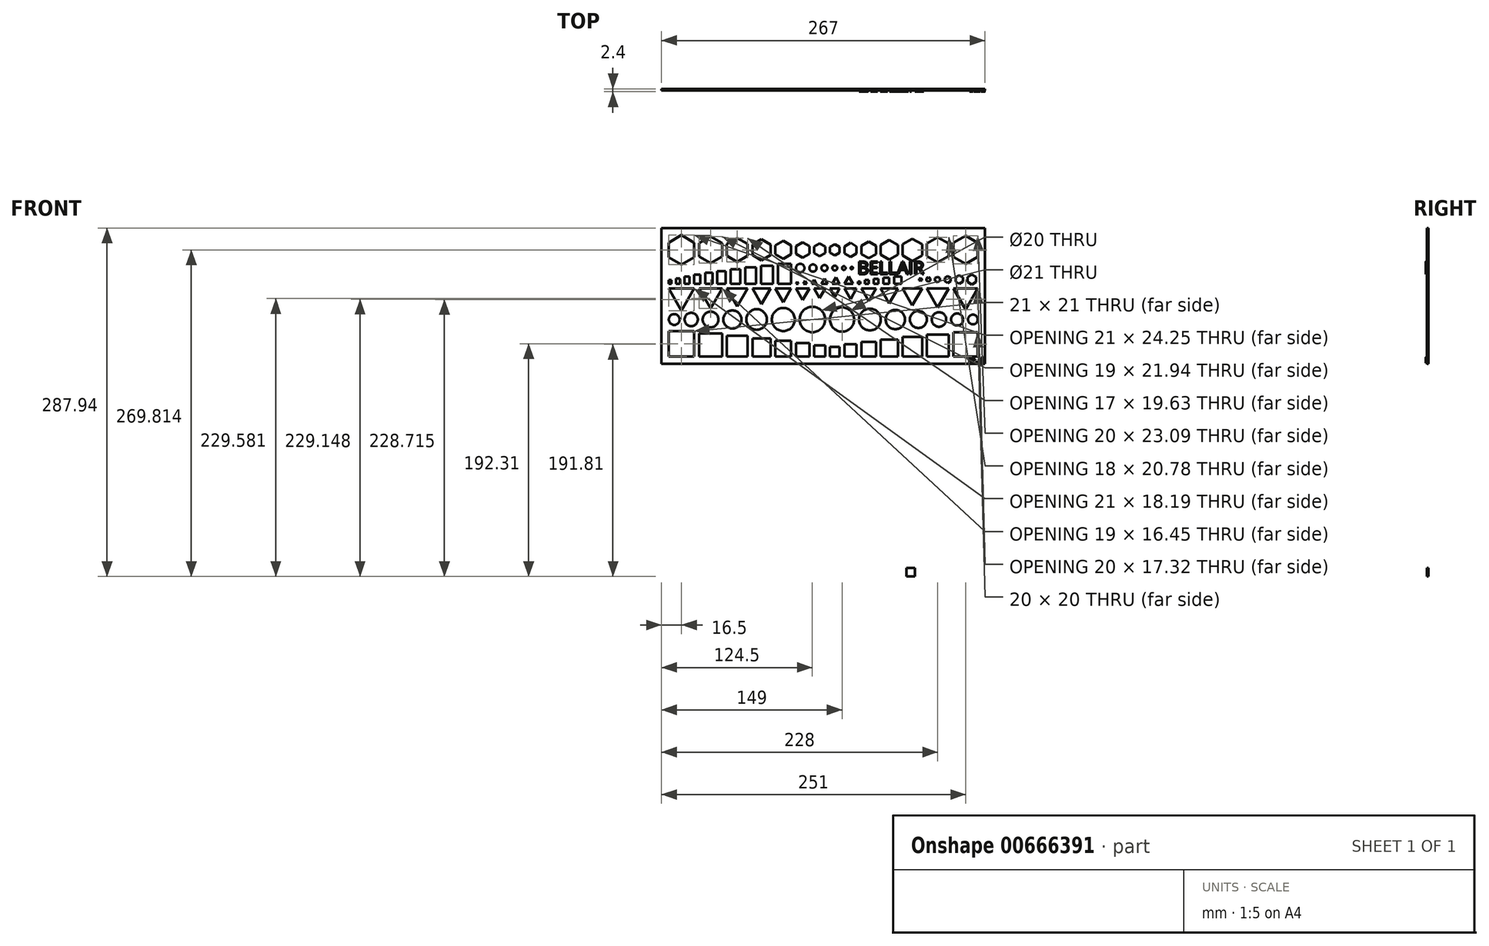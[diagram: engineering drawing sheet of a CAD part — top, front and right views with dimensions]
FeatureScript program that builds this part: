
annotation { "Feature Type Name" : "Feature", "Feature Type Description" : "" }
export const myFeature = defineFeature(function(context is Context, id is Id, definition is map)
    precondition{}
    {
        {
            var Q0;
            Q0=qCreatedBy(makeId("Front.planeOp"),FACE);
            var sketch = newSketch(context, id + "F0", { "sketchPlane" : qUnion([Q0])});
            skLineSegment(sketch, "E0.bottom", {"start": v(0, 0) * mm, "end": v(8, 0) * mm});
            skLineSegment(sketch, "E0.top", {"start": v(0, 8) * mm, "end": v(8, 8) * mm});
            skLineSegment(sketch, "E0.left", {"start": v(0, 0) * mm, "end": v(0, 8) * mm});
            skLineSegment(sketch, "E0.right", {"start": v(8, 0) * mm, "end": v(8, 8) * mm});
            skLineSegment(sketch, "E1.bottom", {"start": v(12, 0) * mm, "end": v(22, 0) * mm});
            skLineSegment(sketch, "E1.top", {"start": v(12, 10) * mm, "end": v(22, 10) * mm});
            skLineSegment(sketch, "E1.left", {"start": v(12, 0) * mm, "end": v(12, 10) * mm});
            skLineSegment(sketch, "E1.right", {"start": v(22, 0) * mm, "end": v(22, 10) * mm});
            skLineSegment(sketch, "E2.bottom", {"start": v(26, 0) * mm, "end": v(38, 0) * mm});
            skLineSegment(sketch, "E2.top", {"start": v(26, 12) * mm, "end": v(38, 12) * mm});
            skLineSegment(sketch, "E2.left", {"start": v(26, 0) * mm, "end": v(26, 12) * mm});
            skLineSegment(sketch, "E2.right", {"start": v(38, 0) * mm, "end": v(38, 12) * mm});
            skLineSegment(sketch, "E3.bottom", {"start": v(42, 0) * mm, "end": v(56, 0) * mm});
            skLineSegment(sketch, "E3.top", {"start": v(42, 14) * mm, "end": v(56, 14) * mm});
            skLineSegment(sketch, "E3.left", {"start": v(42, 0) * mm, "end": v(42, 14) * mm});
            skLineSegment(sketch, "E3.right", {"start": v(56, 0) * mm, "end": v(56, 14) * mm});
            skLineSegment(sketch, "E4.bottom", {"start": v(60, 0) * mm, "end": v(76, 0) * mm});
            skLineSegment(sketch, "E4.top", {"start": v(60, 16) * mm, "end": v(76, 16) * mm});
            skLineSegment(sketch, "E4.left", {"start": v(60, 0) * mm, "end": v(60, 16) * mm});
            skLineSegment(sketch, "E4.right", {"start": v(76, 0) * mm, "end": v(76, 16) * mm});
            skLineSegment(sketch, "E5.bottom", {"start": v(80, 0) * mm, "end": v(98, 0) * mm});
            skLineSegment(sketch, "E5.top", {"start": v(80, 18) * mm, "end": v(98, 18) * mm});
            skLineSegment(sketch, "E5.left", {"start": v(80, 0) * mm, "end": v(80, 18) * mm});
            skLineSegment(sketch, "E5.right", {"start": v(98, 0) * mm, "end": v(98, 18) * mm});
            skLineSegment(sketch, "E6.bottom", {"start": v(102, 0) * mm, "end": v(122, 0) * mm});
            skLineSegment(sketch, "E6.top", {"start": v(102, 20) * mm, "end": v(122, 20) * mm});
            skLineSegment(sketch, "E6.left", {"start": v(102, 0) * mm, "end": v(102, 20) * mm});
            skLineSegment(sketch, "E6.right", {"start": v(122, 0) * mm, "end": v(122, 20) * mm});
            skCircle(sketch, "E7", {"center": v(118, 30.5) * mm, "radius": 4 * mm});
            skCircle(sketch, "E8", {"center": v(105, 30.5) * mm, "radius": 5 * mm});
            skCircle(sketch, "E9", {"center": v(73, 30.5) * mm, "radius": 7 * mm});
            skCircle(sketch, "E10", {"center": v(90, 30.5) * mm, "radius": 6 * mm});
            skCircle(sketch, "E11", {"center": v(54, 30.5) * mm, "radius": 8 * mm});
            skCircle(sketch, "E12", {"center": v(33, 30.5) * mm, "radius": 9 * mm});
            skCircle(sketch, "E13", {"center": v(10, 30.5) * mm, "radius": 10 * mm});
            skLineSegment(sketch, "E14.bottom", {"start": v(-4, 0) * mm, "end": v(-13, 0) * mm});
            skLineSegment(sketch, "E14.top", {"start": v(-4, 9) * mm, "end": v(-13, 9) * mm});
            skLineSegment(sketch, "E14.left", {"start": v(-4, 0) * mm, "end": v(-4, 9) * mm});
            skLineSegment(sketch, "E14.right", {"start": v(-13, 0) * mm, "end": v(-13, 9) * mm});
            skLineSegment(sketch, "E15.bottom", {"start": v(-17, 0) * mm, "end": v(-28, 0) * mm});
            skLineSegment(sketch, "E15.top", {"start": v(-17, 11) * mm, "end": v(-28, 11) * mm});
            skLineSegment(sketch, "E15.left", {"start": v(-17, 0) * mm, "end": v(-17, 11) * mm});
            skLineSegment(sketch, "E15.right", {"start": v(-28, 0) * mm, "end": v(-28, 11) * mm});
            skLineSegment(sketch, "E16.bottom", {"start": v(-32, 0) * mm, "end": v(-45, 0) * mm});
            skLineSegment(sketch, "E16.top", {"start": v(-32, 13) * mm, "end": v(-45, 13) * mm});
            skLineSegment(sketch, "E16.left", {"start": v(-32, 0) * mm, "end": v(-32, 13) * mm});
            skLineSegment(sketch, "E16.right", {"start": v(-45, 0) * mm, "end": v(-45, 13) * mm});
            skLineSegment(sketch, "E17.bottom", {"start": v(-49, 0) * mm, "end": v(-64, 0) * mm});
            skLineSegment(sketch, "E17.top", {"start": v(-49, 15) * mm, "end": v(-64, 15) * mm});
            skLineSegment(sketch, "E17.left", {"start": v(-49, 0) * mm, "end": v(-49, 15) * mm});
            skLineSegment(sketch, "E17.right", {"start": v(-64, 0) * mm, "end": v(-64, 15) * mm});
            skLineSegment(sketch, "E18.bottom", {"start": v(-68, 0) * mm, "end": v(-85, 0) * mm});
            skLineSegment(sketch, "E18.top", {"start": v(-68, 17) * mm, "end": v(-85, 17) * mm});
            skLineSegment(sketch, "E18.left", {"start": v(-68, 0) * mm, "end": v(-68, 17) * mm});
            skLineSegment(sketch, "E18.right", {"start": v(-85, 0) * mm, "end": v(-85, 17) * mm});
            skLineSegment(sketch, "E19.bottom", {"start": v(-89, 0) * mm, "end": v(-108, 0) * mm});
            skLineSegment(sketch, "E19.top", {"start": v(-89, 19) * mm, "end": v(-108, 19) * mm});
            skLineSegment(sketch, "E19.left", {"start": v(-89, 0) * mm, "end": v(-89, 19) * mm});
            skLineSegment(sketch, "E19.right", {"start": v(-108, 0) * mm, "end": v(-108, 19) * mm});
            skLineSegment(sketch, "E20.bottom", {"start": v(-112, 0) * mm, "end": v(-133, 0) * mm});
            skLineSegment(sketch, "E20.top", {"start": v(-112, 21) * mm, "end": v(-133, 21) * mm});
            skLineSegment(sketch, "E20.left", {"start": v(-112, 0) * mm, "end": v(-112, 21) * mm});
            skLineSegment(sketch, "E20.right", {"start": v(-133, 0) * mm, "end": v(-133, 21) * mm});
            skCircle(sketch, "E21", {"center": v(-38.5, 30.5) * mm, "radius": 9.5 * mm});
            skCircle(sketch, "E22", {"center": v(-60.5, 30.5) * mm, "radius": 8.5 * mm});
            skCircle(sketch, "E23", {"center": v(-80.5, 30.5) * mm, "radius": 7.5 * mm});
            skCircle(sketch, "E24", {"center": v(-128.5, 30.5) * mm, "radius": 4.5 * mm});
            skCircle(sketch, "E25", {"center": v(-98.5, 30.5) * mm, "radius": 6.5 * mm});
            skCircle(sketch, "E26", {"center": v(-114.5, 30.5) * mm, "radius": 5.5 * mm});
            skCircle(sketch, "E27", {"center": v(-14.5, 30.5) * mm, "radius": 10.5 * mm});
            skCircle(sketch, "E28.cCircle", {"center": v(4, 53.69) * mm, "radius": 2.3 * mm, "construction": true});
            skLineSegment(sketch, "E28.0", {"start": v(0, 56) * mm, "end": v(8, 56) * mm});
            skLineSegment(sketch, "E28.1", {"start": v(8, 56) * mm, "end": v(4, 49.07) * mm});
            skLineSegment(sketch, "E28.2", {"start": v(4, 49.07) * mm, "end": v(0, 56) * mm});
            skPoint(sketch, "E28.0.midPoint", {"position": v(4, 56) * mm});
            skCircle(sketch, "E29.cCircle", {"center": v(17, 53.11) * mm, "radius": 2.89 * mm, "construction": true});
            skLineSegment(sketch, "E29.0", {"start": v(12, 56) * mm, "end": v(22, 56) * mm});
            skLineSegment(sketch, "E29.1", {"start": v(22, 56) * mm, "end": v(17, 47.34) * mm});
            skLineSegment(sketch, "E29.2", {"start": v(17, 47.34) * mm, "end": v(12, 56) * mm});
            skPoint(sketch, "E29.0.midPoint", {"position": v(17, 56) * mm});
            skCircle(sketch, "E30.cCircle", {"center": v(32, 52.53) * mm, "radius": 3.46 * mm, "construction": true});
            skLineSegment(sketch, "E30.0", {"start": v(26, 56) * mm, "end": v(38, 56) * mm});
            skLineSegment(sketch, "E30.1", {"start": v(38, 56) * mm, "end": v(32, 45.6) * mm});
            skLineSegment(sketch, "E30.2", {"start": v(32, 45.6) * mm, "end": v(26, 56) * mm});
            skPoint(sketch, "E30.0.midPoint", {"position": v(32, 56) * mm});
            skCircle(sketch, "E31.cCircle", {"center": v(49, 51.96) * mm, "radius": 4.04 * mm, "construction": true});
            skLineSegment(sketch, "E31.0", {"start": v(42, 56) * mm, "end": v(56, 56) * mm});
            skLineSegment(sketch, "E31.1", {"start": v(56, 56) * mm, "end": v(49, 43.87) * mm});
            skLineSegment(sketch, "E31.2", {"start": v(49, 43.87) * mm, "end": v(42, 56) * mm});
            skPoint(sketch, "E31.0.midPoint", {"position": v(49, 56) * mm});
            skCircle(sketch, "E32.cCircle", {"center": v(68, 51.38) * mm, "radius": 4.62 * mm, "construction": true});
            skLineSegment(sketch, "E32.0", {"start": v(60, 56) * mm, "end": v(76, 56) * mm});
            skLineSegment(sketch, "E32.1", {"start": v(76, 56) * mm, "end": v(68, 42.14) * mm});
            skLineSegment(sketch, "E32.2", {"start": v(68, 42.14) * mm, "end": v(60, 56) * mm});
            skPoint(sketch, "E32.0.midPoint", {"position": v(68, 56) * mm});
            skCircle(sketch, "E33.cCircle", {"center": v(89, 50.8) * mm, "radius": 5.2 * mm, "construction": true});
            skLineSegment(sketch, "E33.0", {"start": v(80, 56) * mm, "end": v(98, 56) * mm});
            skLineSegment(sketch, "E33.1", {"start": v(98, 56) * mm, "end": v(89, 40.4) * mm});
            skLineSegment(sketch, "E33.2", {"start": v(89, 40.4) * mm, "end": v(80, 56) * mm});
            skPoint(sketch, "E33.0.midPoint", {"position": v(89, 56) * mm});
            skCircle(sketch, "E34.cCircle", {"center": v(112, 50.22) * mm, "radius": 5.77 * mm, "construction": true});
            skLineSegment(sketch, "E34.0", {"start": v(102, 56) * mm, "end": v(122, 56) * mm});
            skLineSegment(sketch, "E34.1", {"start": v(122, 56) * mm, "end": v(112, 38.68) * mm});
            skLineSegment(sketch, "E34.2", {"start": v(112, 38.68) * mm, "end": v(102, 56) * mm});
            skPoint(sketch, "E34.0.midPoint", {"position": v(112, 56) * mm});
            skCircle(sketch, "E35.cCircle", {"center": v(-8.5, 53.4) * mm, "radius": 2.6 * mm, "construction": true});
            skLineSegment(sketch, "E35.0", {"start": v(-13, 56) * mm, "end": v(-4, 56) * mm});
            skLineSegment(sketch, "E35.1", {"start": v(-4, 56) * mm, "end": v(-8.5, 48.2) * mm});
            skLineSegment(sketch, "E35.2", {"start": v(-8.5, 48.2) * mm, "end": v(-13, 56) * mm});
            skPoint(sketch, "E35.0.midPoint", {"position": v(-8.5, 56) * mm});
            skCircle(sketch, "E36.cCircle", {"center": v(-22.5, 52.82) * mm, "radius": 3.18 * mm, "construction": true});
            skLineSegment(sketch, "E36.0", {"start": v(-28, 56) * mm, "end": v(-17, 56) * mm});
            skLineSegment(sketch, "E36.1", {"start": v(-17, 56) * mm, "end": v(-22.5, 46.47) * mm});
            skLineSegment(sketch, "E36.2", {"start": v(-22.5, 46.47) * mm, "end": v(-28, 56) * mm});
            skPoint(sketch, "E36.0.midPoint", {"position": v(-22.5, 56) * mm});
            skCircle(sketch, "E37.cCircle", {"center": v(-38.5, 52.25) * mm, "radius": 3.75 * mm, "construction": true});
            skLineSegment(sketch, "E37.0", {"start": v(-45, 56) * mm, "end": v(-32, 56) * mm});
            skLineSegment(sketch, "E37.1", {"start": v(-32, 56) * mm, "end": v(-38.5, 44.74) * mm});
            skLineSegment(sketch, "E37.2", {"start": v(-38.5, 44.74) * mm, "end": v(-45, 56) * mm});
            skPoint(sketch, "E37.0.midPoint", {"position": v(-38.5, 56) * mm});
            skCircle(sketch, "E38.cCircle", {"center": v(-56.5, 51.67) * mm, "radius": 4.33 * mm, "construction": true});
            skLineSegment(sketch, "E38.0", {"start": v(-64, 56) * mm, "end": v(-49, 56) * mm});
            skLineSegment(sketch, "E38.1", {"start": v(-49, 56) * mm, "end": v(-56.5, 43) * mm});
            skLineSegment(sketch, "E38.2", {"start": v(-56.5, 43) * mm, "end": v(-64, 56) * mm});
            skPoint(sketch, "E38.0.midPoint", {"position": v(-56.5, 56) * mm});
            skCircle(sketch, "E39.cCircle", {"center": v(-76.5, 51.1) * mm, "radius": 4.9 * mm, "construction": true});
            skLineSegment(sketch, "E39.0", {"start": v(-85, 56) * mm, "end": v(-68, 56) * mm});
            skLineSegment(sketch, "E39.1", {"start": v(-68, 56) * mm, "end": v(-76.5, 41.28) * mm});
            skLineSegment(sketch, "E39.2", {"start": v(-76.5, 41.28) * mm, "end": v(-85, 56) * mm});
            skPoint(sketch, "E39.0.midPoint", {"position": v(-76.5, 56) * mm});
            skCircle(sketch, "E40.cCircle", {"center": v(-98.5, 50.51) * mm, "radius": 5.48 * mm, "construction": true});
            skLineSegment(sketch, "E40.0", {"start": v(-108, 56) * mm, "end": v(-89, 56) * mm});
            skLineSegment(sketch, "E40.1", {"start": v(-89, 56) * mm, "end": v(-98.5, 39.54) * mm});
            skLineSegment(sketch, "E40.2", {"start": v(-98.5, 39.54) * mm, "end": v(-108, 56) * mm});
            skPoint(sketch, "E40.0.midPoint", {"position": v(-98.5, 56) * mm});
            skCircle(sketch, "E41.cCircle", {"center": v(-122.5, 49.94) * mm, "radius": 6.06 * mm, "construction": true});
            skLineSegment(sketch, "E41.0", {"start": v(-133, 56) * mm, "end": v(-112, 56) * mm});
            skLineSegment(sketch, "E41.1", {"start": v(-112, 56) * mm, "end": v(-122.5, 37.81) * mm});
            skLineSegment(sketch, "E41.2", {"start": v(-122.5, 37.81) * mm, "end": v(-133, 56) * mm});
            skPoint(sketch, "E41.0.midPoint", {"position": v(-122.5, 56) * mm});
            skLineSegment(sketch, "E42.bottom", {"start": v(-133, 60) * mm, "end": v(-131, 60) * mm});
            skLineSegment(sketch, "E42.top", {"start": v(-133, 63) * mm, "end": v(-131, 63) * mm});
            skLineSegment(sketch, "E42.left", {"start": v(-133, 60) * mm, "end": v(-133, 63) * mm});
            skLineSegment(sketch, "E42.right", {"start": v(-131, 60) * mm, "end": v(-131, 63) * mm});
            skLineSegment(sketch, "E43.bottom", {"start": v(-127, 60) * mm, "end": v(-124, 60) * mm});
            skLineSegment(sketch, "E43.top", {"start": v(-127, 64.5) * mm, "end": v(-124, 64.5) * mm});
            skLineSegment(sketch, "E43.left", {"start": v(-127, 60) * mm, "end": v(-127, 64.5) * mm});
            skLineSegment(sketch, "E43.right", {"start": v(-124, 60) * mm, "end": v(-124, 64.5) * mm});
            skLineSegment(sketch, "E44.bottom", {"start": v(-120, 60) * mm, "end": v(-116, 60) * mm});
            skLineSegment(sketch, "E44.top", {"start": v(-120, 66) * mm, "end": v(-116, 66) * mm});
            skLineSegment(sketch, "E44.left", {"start": v(-120, 60) * mm, "end": v(-120, 66) * mm});
            skLineSegment(sketch, "E44.right", {"start": v(-116, 60) * mm, "end": v(-116, 66) * mm});
            skLineSegment(sketch, "E45.bottom", {"start": v(-112, 60) * mm, "end": v(-107, 60) * mm});
            skLineSegment(sketch, "E45.top", {"start": v(-112, 67.5) * mm, "end": v(-107, 67.5) * mm});
            skLineSegment(sketch, "E45.left", {"start": v(-112, 60) * mm, "end": v(-112, 67.5) * mm});
            skLineSegment(sketch, "E45.right", {"start": v(-107, 60) * mm, "end": v(-107, 67.5) * mm});
            skLineSegment(sketch, "E46.bottom", {"start": v(-103, 60) * mm, "end": v(-97, 60) * mm});
            skLineSegment(sketch, "E46.top", {"start": v(-103, 69) * mm, "end": v(-97, 69) * mm});
            skLineSegment(sketch, "E46.left", {"start": v(-103, 60) * mm, "end": v(-103, 69) * mm});
            skLineSegment(sketch, "E46.right", {"start": v(-97, 60) * mm, "end": v(-97, 69) * mm});
            skLineSegment(sketch, "E47.bottom", {"start": v(-93, 60) * mm, "end": v(-86, 60) * mm});
            skLineSegment(sketch, "E47.top", {"start": v(-93, 70.5) * mm, "end": v(-86, 70.5) * mm});
            skLineSegment(sketch, "E47.left", {"start": v(-93, 60) * mm, "end": v(-93, 70.5) * mm});
            skLineSegment(sketch, "E47.right", {"start": v(-86, 60) * mm, "end": v(-86, 70.5) * mm});
            skLineSegment(sketch, "E48.bottom", {"start": v(-82, 60) * mm, "end": v(-74, 60) * mm});
            skLineSegment(sketch, "E48.top", {"start": v(-82, 72) * mm, "end": v(-74, 72) * mm});
            skLineSegment(sketch, "E48.left", {"start": v(-82, 60) * mm, "end": v(-82, 72) * mm});
            skLineSegment(sketch, "E48.right", {"start": v(-74, 60) * mm, "end": v(-74, 72) * mm});
            skLineSegment(sketch, "E49.bottom", {"start": v(-70, 60) * mm, "end": v(-61, 60) * mm});
            skLineSegment(sketch, "E49.top", {"start": v(-70, 73.5) * mm, "end": v(-61, 73.5) * mm});
            skLineSegment(sketch, "E49.left", {"start": v(-70, 60) * mm, "end": v(-70, 73.5) * mm});
            skLineSegment(sketch, "E49.right", {"start": v(-61, 60) * mm, "end": v(-61, 73.5) * mm});
            skLineSegment(sketch, "E50.bottom", {"start": v(-57, 60) * mm, "end": v(-47, 60) * mm});
            skLineSegment(sketch, "E50.top", {"start": v(-57, 75) * mm, "end": v(-47, 75) * mm});
            skLineSegment(sketch, "E50.left", {"start": v(-57, 60) * mm, "end": v(-57, 75) * mm});
            skLineSegment(sketch, "E50.right", {"start": v(-47, 60) * mm, "end": v(-47, 75) * mm});
            skLineSegment(sketch, "E51.bottom", {"start": v(-43, 60) * mm, "end": v(-32, 60) * mm});
            skLineSegment(sketch, "E51.top", {"start": v(-43, 76.5) * mm, "end": v(-32, 76.5) * mm});
            skLineSegment(sketch, "E51.left", {"start": v(-43, 60) * mm, "end": v(-43, 76.5) * mm});
            skLineSegment(sketch, "E51.right", {"start": v(-32, 60) * mm, "end": v(-32, 76.5) * mm});
            skCircle(sketch, "E52.cCircle", {"center": v(-27, 60.58) * mm, "radius": 0.58 * mm, "construction": true});
            skLineSegment(sketch, "E52.0", {"start": v(-26, 60) * mm, "end": v(-28, 60) * mm});
            skLineSegment(sketch, "E52.1", {"start": v(-28, 60) * mm, "end": v(-27, 61.73) * mm});
            skLineSegment(sketch, "E52.2", {"start": v(-27, 61.73) * mm, "end": v(-26, 60) * mm});
            skPoint(sketch, "E52.0.midPoint", {"position": v(-27, 60) * mm});
            skCircle(sketch, "E53.cCircle", {"center": v(-20.5, 60.86) * mm, "radius": 0.87 * mm, "construction": true});
            skPoint(sketch, "E53.cCircle.perimeterSnap0", {"position": v(-5.5, 60) * mm});
            skLineSegment(sketch, "E53.0", {"start": v(-19, 60) * mm, "end": v(-22, 60) * mm});
            skLineSegment(sketch, "E53.1", {"start": v(-22, 60) * mm, "end": v(-20.5, 62.6) * mm});
            skLineSegment(sketch, "E53.2", {"start": v(-20.5, 62.6) * mm, "end": v(-19, 60) * mm});
            skPoint(sketch, "E53.0.midPoint", {"position": v(-20.5, 60) * mm});
            skPoint(sketch, "E53.0.midPoint.positionSnap0", {"position": v(-5.5, 60) * mm});
            skCircle(sketch, "E54.cCircle", {"center": v(-13, 61.15) * mm, "radius": 1.15 * mm, "construction": true});
            skLineSegment(sketch, "E54.0", {"start": v(-11, 60) * mm, "end": v(-15, 60) * mm});
            skLineSegment(sketch, "E54.1", {"start": v(-15, 60) * mm, "end": v(-13, 63.46) * mm});
            skLineSegment(sketch, "E54.2", {"start": v(-13, 63.46) * mm, "end": v(-11, 60) * mm});
            skPoint(sketch, "E54.0.midPoint", {"position": v(-13, 60) * mm});
            skCircle(sketch, "E55.cCircle", {"center": v(-4.5, 61.44) * mm, "radius": 1.44 * mm, "construction": true});
            skLineSegment(sketch, "E55.0", {"start": v(-2, 60) * mm, "end": v(-7, 60) * mm});
            skLineSegment(sketch, "E55.1", {"start": v(-7, 60) * mm, "end": v(-4.5, 64.33) * mm});
            skLineSegment(sketch, "E55.2", {"start": v(-4.5, 64.33) * mm, "end": v(-2, 60) * mm});
            skPoint(sketch, "E55.0.midPoint", {"position": v(-4.5, 60) * mm});
            skCircle(sketch, "E56.cCircle", {"center": v(5, 61.73) * mm, "radius": 1.73 * mm, "construction": true});
            skLineSegment(sketch, "E56.0", {"start": v(8, 60) * mm, "end": v(2, 60) * mm});
            skLineSegment(sketch, "E56.1", {"start": v(2, 60) * mm, "end": v(5, 65.2) * mm});
            skLineSegment(sketch, "E56.2", {"start": v(5, 65.2) * mm, "end": v(8, 60) * mm});
            skPoint(sketch, "E56.0.midPoint", {"position": v(5, 60) * mm});
            skCircle(sketch, "E57.cCircle", {"center": v(15.5, 62.02) * mm, "radius": 2.02 * mm, "construction": true});
            skLineSegment(sketch, "E57.0", {"start": v(19, 60) * mm, "end": v(12, 60) * mm});
            skLineSegment(sketch, "E57.1", {"start": v(12, 60) * mm, "end": v(15.5, 66.06) * mm});
            skLineSegment(sketch, "E57.2", {"start": v(15.5, 66.06) * mm, "end": v(19, 60) * mm});
            skPoint(sketch, "E57.0.midPoint", {"position": v(15.5, 60) * mm});
            skLineSegment(sketch, "E58", {"start": v(-28, 60) * mm, "end": v(-28, 75.51) * mm});
            skCircle(sketch, "E59", {"center": v(-24.5, 73) * mm, "radius": 3.5 * mm});
            skCircle(sketch, "E60", {"center": v(-14, 73) * mm, "radius": 3 * mm});
            skCircle(sketch, "E61", {"center": v(-4.5, 73) * mm, "radius": 2.5 * mm});
            skCircle(sketch, "E62", {"center": v(4, 73) * mm, "radius": 2 * mm});
            skCircle(sketch, "E63", {"center": v(11.5, 73) * mm, "radius": 1.5 * mm});
            skCircle(sketch, "E64", {"center": v(18, 73) * mm, "radius": 1 * mm});
            skLineSegment(sketch, "E65.bottom", {"start": v(23, 60) * mm, "end": v(25, 60) * mm});
            skLineSegment(sketch, "E65.top", {"start": v(23, 62) * mm, "end": v(25, 62) * mm});
            skLineSegment(sketch, "E65.left", {"start": v(23, 60) * mm, "end": v(23, 62) * mm});
            skLineSegment(sketch, "E65.right", {"start": v(25, 60) * mm, "end": v(25, 62) * mm});
            skLineSegment(sketch, "E66.bottom", {"start": v(29, 60) * mm, "end": v(32, 60) * mm});
            skLineSegment(sketch, "E66.top", {"start": v(29, 63) * mm, "end": v(32, 63) * mm});
            skLineSegment(sketch, "E66.left", {"start": v(29, 60) * mm, "end": v(29, 63) * mm});
            skLineSegment(sketch, "E66.right", {"start": v(32, 60) * mm, "end": v(32, 63) * mm});
            skLineSegment(sketch, "E67.bottom", {"start": v(36, 60) * mm, "end": v(40, 60) * mm});
            skLineSegment(sketch, "E67.top", {"start": v(36, 64) * mm, "end": v(40, 64) * mm});
            skLineSegment(sketch, "E67.left", {"start": v(36, 60) * mm, "end": v(36, 64) * mm});
            skLineSegment(sketch, "E67.right", {"start": v(40, 60) * mm, "end": v(40, 64) * mm});
            skLineSegment(sketch, "E68.bottom", {"start": v(44, 60) * mm, "end": v(49, 60) * mm});
            skLineSegment(sketch, "E68.top", {"start": v(44, 65) * mm, "end": v(49, 65) * mm});
            skLineSegment(sketch, "E68.left", {"start": v(44, 60) * mm, "end": v(44, 65) * mm});
            skLineSegment(sketch, "E68.right", {"start": v(49, 60) * mm, "end": v(49, 65) * mm});
            skLineSegment(sketch, "E69.bottom", {"start": v(53, 60) * mm, "end": v(59, 60) * mm});
            skLineSegment(sketch, "E69.top", {"start": v(53, 66) * mm, "end": v(59, 66) * mm});
            skLineSegment(sketch, "E69.left", {"start": v(53, 60) * mm, "end": v(53, 66) * mm});
            skLineSegment(sketch, "E69.right", {"start": v(59, 60) * mm, "end": v(59, 66) * mm});
            skLineSegment(sketch, "E70.bottom", {"start": v(63, -181.81) * mm, "end": v(70, -181.81) * mm});
            skLineSegment(sketch, "E70.top", {"start": v(63, -174.81) * mm, "end": v(70, -174.81) * mm});
            skLineSegment(sketch, "E70.left", {"start": v(63, -181.81) * mm, "end": v(63, -174.81) * mm});
            skLineSegment(sketch, "E70.right", {"start": v(70, -181.81) * mm, "end": v(70, -174.81) * mm});
            skCircle(sketch, "E71.cCircle", {"center": v(74.74, 63.5) * mm, "radius": 1 * mm, "construction": true});
            skLineSegment(sketch, "E71.0", {"start": v(75.73, 64.08) * mm, "end": v(75.74, 62.92) * mm});
            skLineSegment(sketch, "E71.1", {"start": v(75.74, 62.92) * mm, "end": v(74.74, 62.34) * mm});
            skLineSegment(sketch, "E71.2", {"start": v(74.74, 62.34) * mm, "end": v(73.74, 62.92) * mm});
            skLineSegment(sketch, "E71.3", {"start": v(73.74, 62.92) * mm, "end": v(73.73, 64.07) * mm});
            skLineSegment(sketch, "E71.4", {"start": v(73.73, 64.07) * mm, "end": v(74.73, 64.65) * mm});
            skLineSegment(sketch, "E71.5", {"start": v(74.73, 64.65) * mm, "end": v(75.73, 64.08) * mm});
            skPoint(sketch, "E71.0.midPoint", {"position": v(75.74, 63.5) * mm});
            skCircle(sketch, "E72.cCircle", {"center": v(81.24, 63.5) * mm, "radius": 1.5 * mm, "construction": true});
            skLineSegment(sketch, "E72.0", {"start": v(82.73, 64.37) * mm, "end": v(82.74, 62.63) * mm});
            skLineSegment(sketch, "E72.1", {"start": v(82.74, 62.63) * mm, "end": v(81.24, 61.77) * mm});
            skLineSegment(sketch, "E72.2", {"start": v(81.24, 61.77) * mm, "end": v(79.74, 62.63) * mm});
            skLineSegment(sketch, "E72.3", {"start": v(79.74, 62.63) * mm, "end": v(79.73, 64.36) * mm});
            skLineSegment(sketch, "E72.4", {"start": v(79.73, 64.36) * mm, "end": v(81.23, 65.23) * mm});
            skLineSegment(sketch, "E72.5", {"start": v(81.23, 65.23) * mm, "end": v(82.73, 64.37) * mm});
            skPoint(sketch, "E72.0.midPoint", {"position": v(82.74, 63.5) * mm});
            skCircle(sketch, "E73.cCircle", {"center": v(88.74, 63.5) * mm, "radius": 2 * mm, "construction": true});
            skLineSegment(sketch, "E73.0", {"start": v(86.74, 62.34) * mm, "end": v(86.73, 64.65) * mm});
            skLineSegment(sketch, "E73.1", {"start": v(86.73, 64.65) * mm, "end": v(88.73, 65.8) * mm});
            skLineSegment(sketch, "E73.2", {"start": v(88.73, 65.8) * mm, "end": v(90.73, 64.66) * mm});
            skLineSegment(sketch, "E73.3", {"start": v(90.73, 64.66) * mm, "end": v(90.74, 62.35) * mm});
            skLineSegment(sketch, "E73.4", {"start": v(90.74, 62.35) * mm, "end": v(88.74, 61.19) * mm});
            skLineSegment(sketch, "E73.5", {"start": v(88.74, 61.19) * mm, "end": v(86.74, 62.34) * mm});
            skPoint(sketch, "E73.0.midPoint", {"position": v(86.74, 63.5) * mm});
            skCircle(sketch, "E74.cCircle", {"center": v(97.24, 63.5) * mm, "radius": 2.5 * mm, "construction": true});
            skLineSegment(sketch, "E74.0", {"start": v(99.73, 64.94) * mm, "end": v(99.74, 62.06) * mm});
            skLineSegment(sketch, "E74.1", {"start": v(99.74, 62.06) * mm, "end": v(97.24, 60.61) * mm});
            skLineSegment(sketch, "E74.2", {"start": v(97.24, 60.61) * mm, "end": v(94.74, 62.05) * mm});
            skLineSegment(sketch, "E74.3", {"start": v(94.74, 62.05) * mm, "end": v(94.73, 64.94) * mm});
            skLineSegment(sketch, "E74.4", {"start": v(94.73, 64.94) * mm, "end": v(97.23, 66.38) * mm});
            skLineSegment(sketch, "E74.5", {"start": v(97.23, 66.38) * mm, "end": v(99.73, 64.94) * mm});
            skPoint(sketch, "E74.0.midPoint", {"position": v(99.74, 63.5) * mm});
            skCircle(sketch, "E75.cCircle", {"center": v(106.74, 63.5) * mm, "radius": 3 * mm, "construction": true});
            skLineSegment(sketch, "E75.0", {"start": v(109.73, 65.23) * mm, "end": v(109.74, 61.77) * mm});
            skLineSegment(sketch, "E75.1", {"start": v(109.74, 61.77) * mm, "end": v(106.74, 60.03) * mm});
            skLineSegment(sketch, "E75.2", {"start": v(106.74, 60.03) * mm, "end": v(103.74, 61.76) * mm});
            skLineSegment(sketch, "E75.3", {"start": v(103.74, 61.76) * mm, "end": v(103.73, 65.23) * mm});
            skLineSegment(sketch, "E75.4", {"start": v(103.73, 65.23) * mm, "end": v(106.73, 66.96) * mm});
            skLineSegment(sketch, "E75.5", {"start": v(106.73, 66.96) * mm, "end": v(109.73, 65.23) * mm});
            skPoint(sketch, "E75.0.midPoint", {"position": v(109.74, 63.5) * mm});
            skCircle(sketch, "E76.cCircle", {"center": v(117.24, 63.5) * mm, "radius": 3.5 * mm, "construction": true});
            skLineSegment(sketch, "E76.0", {"start": v(120.73, 65.52) * mm, "end": v(120.74, 61.48) * mm});
            skLineSegment(sketch, "E76.1", {"start": v(120.74, 61.48) * mm, "end": v(117.24, 59.46) * mm});
            skLineSegment(sketch, "E76.2", {"start": v(117.24, 59.46) * mm, "end": v(113.74, 61.47) * mm});
            skLineSegment(sketch, "E76.3", {"start": v(113.74, 61.47) * mm, "end": v(113.73, 65.51) * mm});
            skLineSegment(sketch, "E76.4", {"start": v(113.73, 65.51) * mm, "end": v(117.23, 67.54) * mm});
            skLineSegment(sketch, "E76.5", {"start": v(117.23, 67.54) * mm, "end": v(120.73, 65.52) * mm});
            skPoint(sketch, "E76.0.midPoint", {"position": v(120.74, 63.5) * mm});
            skCircle(sketch, "E77.cCircle", {"center": v(4, 88) * mm, "radius": 4 * mm, "construction": true});
            skLineSegment(sketch, "E77.0", {"start": v(0, 85.7) * mm, "end": v(0, 90.31) * mm});
            skLineSegment(sketch, "E77.1", {"start": v(0, 90.31) * mm, "end": v(4, 92.62) * mm});
            skLineSegment(sketch, "E77.2", {"start": v(4, 92.62) * mm, "end": v(8, 90.31) * mm});
            skLineSegment(sketch, "E77.3", {"start": v(8, 90.31) * mm, "end": v(8, 85.7) * mm});
            skLineSegment(sketch, "E77.4", {"start": v(8, 85.7) * mm, "end": v(4, 83.38) * mm});
            skLineSegment(sketch, "E77.5", {"start": v(4, 83.38) * mm, "end": v(0, 85.7) * mm});
            skPoint(sketch, "E77.0.midPoint", {"position": v(0, 88) * mm});
            skCircle(sketch, "E78.cCircle", {"center": v(17, 88) * mm, "radius": 5 * mm, "construction": true});
            skLineSegment(sketch, "E78.0", {"start": v(22, 90.9) * mm, "end": v(22, 85.12) * mm});
            skLineSegment(sketch, "E78.1", {"start": v(22, 85.12) * mm, "end": v(17, 82.23) * mm});
            skLineSegment(sketch, "E78.2", {"start": v(17, 82.23) * mm, "end": v(12, 85.12) * mm});
            skLineSegment(sketch, "E78.3", {"start": v(12, 85.12) * mm, "end": v(12, 90.9) * mm});
            skLineSegment(sketch, "E78.4", {"start": v(12, 90.9) * mm, "end": v(17, 93.78) * mm});
            skLineSegment(sketch, "E78.5", {"start": v(17, 93.78) * mm, "end": v(22, 90.9) * mm});
            skPoint(sketch, "E78.0.midPoint", {"position": v(22, 88) * mm});
            skCircle(sketch, "E79.cCircle", {"center": v(32, 88) * mm, "radius": 6 * mm, "construction": true});
            skLineSegment(sketch, "E79.0", {"start": v(26, 84.54) * mm, "end": v(26, 91.47) * mm});
            skLineSegment(sketch, "E79.1", {"start": v(26, 91.47) * mm, "end": v(32, 94.93) * mm});
            skLineSegment(sketch, "E79.2", {"start": v(32, 94.93) * mm, "end": v(38, 91.47) * mm});
            skLineSegment(sketch, "E79.3", {"start": v(38, 91.47) * mm, "end": v(38, 84.54) * mm});
            skLineSegment(sketch, "E79.4", {"start": v(38, 84.54) * mm, "end": v(32, 81.08) * mm});
            skLineSegment(sketch, "E79.5", {"start": v(32, 81.08) * mm, "end": v(26, 84.54) * mm});
            skPoint(sketch, "E79.0.midPoint", {"position": v(26, 88) * mm});
            skCircle(sketch, "E80.cCircle", {"center": v(49, 88) * mm, "radius": 7 * mm, "construction": true});
            skLineSegment(sketch, "E80.0", {"start": v(42, 83.96) * mm, "end": v(42, 92.05) * mm});
            skLineSegment(sketch, "E80.1", {"start": v(42, 92.05) * mm, "end": v(49, 96.09) * mm});
            skLineSegment(sketch, "E80.2", {"start": v(49, 96.09) * mm, "end": v(56, 92.05) * mm});
            skLineSegment(sketch, "E80.3", {"start": v(56, 92.05) * mm, "end": v(56, 83.96) * mm});
            skLineSegment(sketch, "E80.4", {"start": v(56, 83.96) * mm, "end": v(49, 79.92) * mm});
            skLineSegment(sketch, "E80.5", {"start": v(49, 79.92) * mm, "end": v(42, 83.96) * mm});
            skPoint(sketch, "E80.0.midPoint", {"position": v(42, 88) * mm});
            skCircle(sketch, "E81.cCircle", {"center": v(68, 88) * mm, "radius": 8 * mm, "construction": true});
            skLineSegment(sketch, "E81.0", {"start": v(60, 83.38) * mm, "end": v(60, 92.62) * mm});
            skLineSegment(sketch, "E81.1", {"start": v(60, 92.62) * mm, "end": v(68, 97.24) * mm});
            skLineSegment(sketch, "E81.2", {"start": v(68, 97.24) * mm, "end": v(76, 92.62) * mm});
            skLineSegment(sketch, "E81.3", {"start": v(76, 92.62) * mm, "end": v(76, 83.38) * mm});
            skLineSegment(sketch, "E81.4", {"start": v(76, 83.38) * mm, "end": v(68, 78.77) * mm});
            skLineSegment(sketch, "E81.5", {"start": v(68, 78.77) * mm, "end": v(60, 83.38) * mm});
            skPoint(sketch, "E81.0.midPoint", {"position": v(60, 88) * mm});
            skCircle(sketch, "E82.cCircle", {"center": v(89, 88) * mm, "radius": 9 * mm, "construction": true});
            skLineSegment(sketch, "E82.0", {"start": v(80, 82.8) * mm, "end": v(80, 93.2) * mm});
            skLineSegment(sketch, "E82.1", {"start": v(80, 93.2) * mm, "end": v(89, 98.4) * mm});
            skLineSegment(sketch, "E82.2", {"start": v(89, 98.4) * mm, "end": v(98, 93.2) * mm});
            skLineSegment(sketch, "E82.3", {"start": v(98, 93.2) * mm, "end": v(98, 82.8) * mm});
            skLineSegment(sketch, "E82.4", {"start": v(98, 82.8) * mm, "end": v(89, 77.61) * mm});
            skLineSegment(sketch, "E82.5", {"start": v(89, 77.61) * mm, "end": v(80, 82.8) * mm});
            skPoint(sketch, "E82.0.midPoint", {"position": v(80, 88) * mm});
            skCircle(sketch, "E83.cCircle", {"center": v(112, 88) * mm, "radius": 10 * mm, "construction": true});
            skLineSegment(sketch, "E83.0", {"start": v(102, 82.23) * mm, "end": v(102, 93.78) * mm});
            skLineSegment(sketch, "E83.1", {"start": v(102, 93.78) * mm, "end": v(112, 99.55) * mm});
            skLineSegment(sketch, "E83.2", {"start": v(112, 99.55) * mm, "end": v(122, 93.78) * mm});
            skLineSegment(sketch, "E83.3", {"start": v(122, 93.78) * mm, "end": v(122, 82.23) * mm});
            skLineSegment(sketch, "E83.4", {"start": v(122, 82.23) * mm, "end": v(112, 76.46) * mm});
            skLineSegment(sketch, "E83.5", {"start": v(112, 76.46) * mm, "end": v(102, 82.23) * mm});
            skPoint(sketch, "E83.0.midPoint", {"position": v(102, 88) * mm});
            skCircle(sketch, "E84.cCircle", {"center": v(-8.5, 88) * mm, "radius": 4.5 * mm, "construction": true});
            skLineSegment(sketch, "E84.0", {"start": v(-13, 85.4) * mm, "end": v(-13, 90.6) * mm});
            skLineSegment(sketch, "E84.1", {"start": v(-13, 90.6) * mm, "end": v(-8.5, 93.2) * mm});
            skLineSegment(sketch, "E84.2", {"start": v(-8.5, 93.2) * mm, "end": v(-4, 90.6) * mm});
            skLineSegment(sketch, "E84.3", {"start": v(-4, 90.6) * mm, "end": v(-4, 85.4) * mm});
            skLineSegment(sketch, "E84.4", {"start": v(-4, 85.4) * mm, "end": v(-8.5, 82.8) * mm});
            skLineSegment(sketch, "E84.5", {"start": v(-8.5, 82.8) * mm, "end": v(-13, 85.4) * mm});
            skPoint(sketch, "E84.0.midPoint", {"position": v(-13, 88) * mm});
            skCircle(sketch, "E85.cCircle", {"center": v(-22.5, 88) * mm, "radius": 5.5 * mm, "construction": true});
            skLineSegment(sketch, "E85.0", {"start": v(-28, 84.83) * mm, "end": v(-28, 91.18) * mm});
            skLineSegment(sketch, "E85.1", {"start": v(-28, 91.18) * mm, "end": v(-22.5, 94.35) * mm});
            skLineSegment(sketch, "E85.2", {"start": v(-22.5, 94.35) * mm, "end": v(-17, 91.18) * mm});
            skLineSegment(sketch, "E85.3", {"start": v(-17, 91.18) * mm, "end": v(-17, 84.83) * mm});
            skLineSegment(sketch, "E85.4", {"start": v(-17, 84.83) * mm, "end": v(-22.5, 81.65) * mm});
            skLineSegment(sketch, "E85.5", {"start": v(-22.5, 81.65) * mm, "end": v(-28, 84.83) * mm});
            skPoint(sketch, "E85.0.midPoint", {"position": v(-28, 88) * mm});
            skCircle(sketch, "E86.cCircle", {"center": v(-38.5, 88) * mm, "radius": 6.5 * mm, "construction": true});
            skLineSegment(sketch, "E86.0", {"start": v(-32, 91.76) * mm, "end": v(-32, 84.25) * mm});
            skLineSegment(sketch, "E86.1", {"start": v(-32, 84.25) * mm, "end": v(-38.5, 80.5) * mm});
            skLineSegment(sketch, "E86.2", {"start": v(-38.5, 80.5) * mm, "end": v(-45, 84.25) * mm});
            skLineSegment(sketch, "E86.3", {"start": v(-45, 84.25) * mm, "end": v(-45, 91.76) * mm});
            skLineSegment(sketch, "E86.4", {"start": v(-45, 91.76) * mm, "end": v(-38.5, 95.5) * mm});
            skLineSegment(sketch, "E86.5", {"start": v(-38.5, 95.5) * mm, "end": v(-32, 91.76) * mm});
            skPoint(sketch, "E86.0.midPoint", {"position": v(-32, 88) * mm});
            skCircle(sketch, "E87.cCircle", {"center": v(-56.5, 88) * mm, "radius": 7.5 * mm, "construction": true});
            skLineSegment(sketch, "E87.0", {"start": v(-49, 92.33) * mm, "end": v(-49, 83.67) * mm});
            skLineSegment(sketch, "E87.1", {"start": v(-49, 83.67) * mm, "end": v(-56.5, 79.34) * mm});
            skLineSegment(sketch, "E87.2", {"start": v(-56.5, 79.34) * mm, "end": v(-64, 83.67) * mm});
            skLineSegment(sketch, "E87.3", {"start": v(-64, 83.67) * mm, "end": v(-64, 92.33) * mm});
            skLineSegment(sketch, "E87.4", {"start": v(-64, 92.33) * mm, "end": v(-56.5, 96.66) * mm});
            skLineSegment(sketch, "E87.5", {"start": v(-56.5, 96.66) * mm, "end": v(-49, 92.33) * mm});
            skPoint(sketch, "E87.0.midPoint", {"position": v(-49, 88) * mm});
            skCircle(sketch, "E88.cCircle", {"center": v(-76.5, 88) * mm, "radius": 8.5 * mm, "construction": true});
            skLineSegment(sketch, "E88.0", {"start": v(-85, 83.1) * mm, "end": v(-85, 92.91) * mm});
            skLineSegment(sketch, "E88.1", {"start": v(-85, 92.91) * mm, "end": v(-76.5, 97.82) * mm});
            skLineSegment(sketch, "E88.2", {"start": v(-76.5, 97.82) * mm, "end": v(-68, 92.91) * mm});
            skLineSegment(sketch, "E88.3", {"start": v(-68, 92.91) * mm, "end": v(-68, 83.1) * mm});
            skLineSegment(sketch, "E88.4", {"start": v(-68, 83.1) * mm, "end": v(-76.5, 78.19) * mm});
            skLineSegment(sketch, "E88.5", {"start": v(-76.5, 78.19) * mm, "end": v(-85, 83.1) * mm});
            skPoint(sketch, "E88.0.midPoint", {"position": v(-85, 88) * mm});
            skCircle(sketch, "E89.cCircle", {"center": v(-98.5, 88) * mm, "radius": 9.5 * mm, "construction": true});
            skLineSegment(sketch, "E89.0", {"start": v(-108, 82.52) * mm, "end": v(-108, 93.49) * mm});
            skLineSegment(sketch, "E89.1", {"start": v(-108, 93.49) * mm, "end": v(-98.5, 98.97) * mm});
            skLineSegment(sketch, "E89.2", {"start": v(-98.5, 98.97) * mm, "end": v(-89, 93.49) * mm});
            skLineSegment(sketch, "E89.3", {"start": v(-89, 93.49) * mm, "end": v(-89, 82.52) * mm});
            skLineSegment(sketch, "E89.4", {"start": v(-89, 82.52) * mm, "end": v(-98.5, 77.03) * mm});
            skLineSegment(sketch, "E89.5", {"start": v(-98.5, 77.03) * mm, "end": v(-108, 82.52) * mm});
            skPoint(sketch, "E89.0.midPoint", {"position": v(-108, 88) * mm});
            skCircle(sketch, "E90.cCircle", {"center": v(-122.5, 88) * mm, "radius": 10.5 * mm, "construction": true});
            skLineSegment(sketch, "E90.0", {"start": v(-112, 94.07) * mm, "end": v(-112, 81.94) * mm});
            skLineSegment(sketch, "E90.1", {"start": v(-112, 81.94) * mm, "end": v(-122.5, 75.88) * mm});
            skLineSegment(sketch, "E90.2", {"start": v(-122.5, 75.88) * mm, "end": v(-133, 81.94) * mm});
            skLineSegment(sketch, "E90.3", {"start": v(-133, 81.94) * mm, "end": v(-133, 94.07) * mm});
            skLineSegment(sketch, "E90.4", {"start": v(-133, 94.07) * mm, "end": v(-122.5, 100.13) * mm});
            skLineSegment(sketch, "E90.5", {"start": v(-122.5, 100.13) * mm, "end": v(-112, 94.07) * mm});
            skPoint(sketch, "E90.0.midPoint", {"position": v(-112, 88) * mm});
            skLineSegment(sketch, "E91.bottom", {"start": v(-139, 106.13) * mm, "end": v(128, 106.13) * mm});
            skLineSegment(sketch, "E91.top", {"start": v(-139, -6) * mm, "end": v(128, -6) * mm});
            skLineSegment(sketch, "E91.left", {"start": v(-139, 106.13) * mm, "end": v(-139, -6) * mm});
            skLineSegment(sketch, "E91.right", {"start": v(128, 106.13) * mm, "end": v(128, -6) * mm});
            skSolve(sketch);
        }
        {
            var Q0;
            Q0=qSketchRegion(id+"F0",true);
            extrude(context, id + "F1", {"entities" : qUnion([Q0]), "depth" : 1.4 * mm, "offsetDistance" : 25 * mm});
        }
        {
            var Q0;
            Q0=makeQuery(id+"F1.opExtrude","CAP_FACE",FACE,{"disambiguationData":[OSD([sQuery(id+"F0.wireOp",EDGE,"E0.bottom"),sQuery(id+"F0.wireOp",EDGE,"E0.top"),sQuery(id+"F0.wireOp",EDGE,"E0.left"),sQuery(id+"F0.wireOp",EDGE,"E0.right"),sQuery(id+"F0.wireOp",EDGE,"E1.bottom"),sQuery(id+"F0.wireOp",EDGE,"E1.top"),sQuery(id+"F0.wireOp",EDGE,"E1.left"),sQuery(id+"F0.wireOp",EDGE,"E1.right"),sQuery(id+"F0.wireOp",EDGE,"E2.bottom"),sQuery(id+"F0.wireOp",EDGE,"E2.top"),sQuery(id+"F0.wireOp",EDGE,"E2.left"),sQuery(id+"F0.wireOp",EDGE,"E2.right"),sQuery(id+"F0.wireOp",EDGE,"E3.bottom"),sQuery(id+"F0.wireOp",EDGE,"E3.top"),sQuery(id+"F0.wireOp",EDGE,"E3.left"),sQuery(id+"F0.wireOp",EDGE,"E3.right"),sQuery(id+"F0.wireOp",EDGE,"E4.bottom"),sQuery(id+"F0.wireOp",EDGE,"E4.top"),sQuery(id+"F0.wireOp",EDGE,"E4.left"),sQuery(id+"F0.wireOp",EDGE,"E4.right"),sQuery(id+"F0.wireOp",EDGE,"E5.bottom"),sQuery(id+"F0.wireOp",EDGE,"E5.top"),sQuery(id+"F0.wireOp",EDGE,"E5.left"),sQuery(id+"F0.wireOp",EDGE,"E5.right"),sQuery(id+"F0.wireOp",EDGE,"E6.bottom"),sQuery(id+"F0.wireOp",EDGE,"E6.top"),sQuery(id+"F0.wireOp",EDGE,"E6.left"),sQuery(id+"F0.wireOp",EDGE,"E6.right"),sQuery(id+"F0.wireOp",EDGE,"E7"),sQuery(id+"F0.wireOp",EDGE,"E8"),sQuery(id+"F0.wireOp",EDGE,"E9"),sQuery(id+"F0.wireOp",EDGE,"E10"),sQuery(id+"F0.wireOp",EDGE,"E11"),sQuery(id+"F0.wireOp",EDGE,"E12"),sQuery(id+"F0.wireOp",EDGE,"E13"),sQuery(id+"F0.wireOp",EDGE,"E14.bottom"),sQuery(id+"F0.wireOp",EDGE,"E14.top"),sQuery(id+"F0.wireOp",EDGE,"E14.left"),sQuery(id+"F0.wireOp",EDGE,"E14.right"),sQuery(id+"F0.wireOp",EDGE,"E15.bottom"),sQuery(id+"F0.wireOp",EDGE,"E15.top"),sQuery(id+"F0.wireOp",EDGE,"E15.left"),sQuery(id+"F0.wireOp",EDGE,"E15.right"),sQuery(id+"F0.wireOp",EDGE,"E16.bottom"),sQuery(id+"F0.wireOp",EDGE,"E16.top"),sQuery(id+"F0.wireOp",EDGE,"E16.left"),sQuery(id+"F0.wireOp",EDGE,"E16.right"),sQuery(id+"F0.wireOp",EDGE,"E17.bottom"),sQuery(id+"F0.wireOp",EDGE,"E17.top"),sQuery(id+"F0.wireOp",EDGE,"E17.left"),sQuery(id+"F0.wireOp",EDGE,"E17.right"),sQuery(id+"F0.wireOp",EDGE,"E18.bottom"),sQuery(id+"F0.wireOp",EDGE,"E18.top"),sQuery(id+"F0.wireOp",EDGE,"E18.left"),sQuery(id+"F0.wireOp",EDGE,"E18.right"),sQuery(id+"F0.wireOp",EDGE,"E19.bottom"),sQuery(id+"F0.wireOp",EDGE,"E19.top"),sQuery(id+"F0.wireOp",EDGE,"E19.left"),sQuery(id+"F0.wireOp",EDGE,"E19.right"),sQuery(id+"F0.wireOp",EDGE,"E20.bottom"),sQuery(id+"F0.wireOp",EDGE,"E20.top"),sQuery(id+"F0.wireOp",EDGE,"E20.left"),sQuery(id+"F0.wireOp",EDGE,"E20.right"),sQuery(id+"F0.wireOp",EDGE,"E21"),sQuery(id+"F0.wireOp",EDGE,"E22"),sQuery(id+"F0.wireOp",EDGE,"E23"),sQuery(id+"F0.wireOp",EDGE,"E24"),sQuery(id+"F0.wireOp",EDGE,"E25"),sQuery(id+"F0.wireOp",EDGE,"E26"),sQuery(id+"F0.wireOp",EDGE,"E27"),sQuery(id+"F0.wireOp",EDGE,"E28.0"),sQuery(id+"F0.wireOp",EDGE,"E28.1"),sQuery(id+"F0.wireOp",EDGE,"E28.2"),sQuery(id+"F0.wireOp",EDGE,"E29.0"),sQuery(id+"F0.wireOp",EDGE,"E29.1"),sQuery(id+"F0.wireOp",EDGE,"E29.2"),sQuery(id+"F0.wireOp",EDGE,"E30.0"),sQuery(id+"F0.wireOp",EDGE,"E30.1"),sQuery(id+"F0.wireOp",EDGE,"E30.2"),sQuery(id+"F0.wireOp",EDGE,"E31.0"),sQuery(id+"F0.wireOp",EDGE,"E31.1"),sQuery(id+"F0.wireOp",EDGE,"E31.2"),sQuery(id+"F0.wireOp",EDGE,"E32.0"),sQuery(id+"F0.wireOp",EDGE,"E32.1"),sQuery(id+"F0.wireOp",EDGE,"E32.2"),sQuery(id+"F0.wireOp",EDGE,"E33.0"),sQuery(id+"F0.wireOp",EDGE,"E33.1"),sQuery(id+"F0.wireOp",EDGE,"E33.2"),sQuery(id+"F0.wireOp",EDGE,"E34.0"),sQuery(id+"F0.wireOp",EDGE,"E34.1"),sQuery(id+"F0.wireOp",EDGE,"E34.2"),sQuery(id+"F0.wireOp",EDGE,"E35.0"),sQuery(id+"F0.wireOp",EDGE,"E35.1"),sQuery(id+"F0.wireOp",EDGE,"E35.2"),sQuery(id+"F0.wireOp",EDGE,"E36.0"),sQuery(id+"F0.wireOp",EDGE,"E36.1"),sQuery(id+"F0.wireOp",EDGE,"E36.2"),sQuery(id+"F0.wireOp",EDGE,"E37.0"),sQuery(id+"F0.wireOp",EDGE,"E37.1"),sQuery(id+"F0.wireOp",EDGE,"E37.2"),sQuery(id+"F0.wireOp",EDGE,"E38.0"),sQuery(id+"F0.wireOp",EDGE,"E38.1"),sQuery(id+"F0.wireOp",EDGE,"E38.2"),sQuery(id+"F0.wireOp",EDGE,"E39.0"),sQuery(id+"F0.wireOp",EDGE,"E39.1"),sQuery(id+"F0.wireOp",EDGE,"E39.2"),sQuery(id+"F0.wireOp",EDGE,"E40.0"),sQuery(id+"F0.wireOp",EDGE,"E40.1"),sQuery(id+"F0.wireOp",EDGE,"E40.2"),sQuery(id+"F0.wireOp",EDGE,"E41.0"),sQuery(id+"F0.wireOp",EDGE,"E41.1"),sQuery(id+"F0.wireOp",EDGE,"E41.2"),sQuery(id+"F0.wireOp",EDGE,"E42.bottom"),sQuery(id+"F0.wireOp",EDGE,"E42.top"),sQuery(id+"F0.wireOp",EDGE,"E42.left"),sQuery(id+"F0.wireOp",EDGE,"E42.right"),sQuery(id+"F0.wireOp",EDGE,"E43.bottom"),sQuery(id+"F0.wireOp",EDGE,"E43.top"),sQuery(id+"F0.wireOp",EDGE,"E43.left"),sQuery(id+"F0.wireOp",EDGE,"E43.right"),sQuery(id+"F0.wireOp",EDGE,"E44.bottom"),sQuery(id+"F0.wireOp",EDGE,"E44.top"),sQuery(id+"F0.wireOp",EDGE,"E44.left"),sQuery(id+"F0.wireOp",EDGE,"E44.right"),sQuery(id+"F0.wireOp",EDGE,"E45.bottom"),sQuery(id+"F0.wireOp",EDGE,"E45.top"),sQuery(id+"F0.wireOp",EDGE,"E45.left"),sQuery(id+"F0.wireOp",EDGE,"E45.right"),sQuery(id+"F0.wireOp",EDGE,"E46.bottom"),sQuery(id+"F0.wireOp",EDGE,"E46.top"),sQuery(id+"F0.wireOp",EDGE,"E46.left"),sQuery(id+"F0.wireOp",EDGE,"E46.right"),sQuery(id+"F0.wireOp",EDGE,"E47.bottom"),sQuery(id+"F0.wireOp",EDGE,"E47.top"),sQuery(id+"F0.wireOp",EDGE,"E47.left"),sQuery(id+"F0.wireOp",EDGE,"E47.right"),sQuery(id+"F0.wireOp",EDGE,"E48.bottom"),sQuery(id+"F0.wireOp",EDGE,"E48.top"),sQuery(id+"F0.wireOp",EDGE,"E48.left"),sQuery(id+"F0.wireOp",EDGE,"E48.right"),sQuery(id+"F0.wireOp",EDGE,"E49.bottom"),sQuery(id+"F0.wireOp",EDGE,"E49.top"),sQuery(id+"F0.wireOp",EDGE,"E49.left"),sQuery(id+"F0.wireOp",EDGE,"E49.right"),sQuery(id+"F0.wireOp",EDGE,"E50.bottom"),sQuery(id+"F0.wireOp",EDGE,"E50.top"),sQuery(id+"F0.wireOp",EDGE,"E50.left"),sQuery(id+"F0.wireOp",EDGE,"E50.right"),sQuery(id+"F0.wireOp",EDGE,"E51.bottom"),sQuery(id+"F0.wireOp",EDGE,"E51.top"),sQuery(id+"F0.wireOp",EDGE,"E51.left"),sQuery(id+"F0.wireOp",EDGE,"E51.right"),sQuery(id+"F0.wireOp",EDGE,"E52.0"),sQuery(id+"F0.wireOp",EDGE,"E52.1"),sQuery(id+"F0.wireOp",EDGE,"E52.2"),sQuery(id+"F0.wireOp",EDGE,"E53.0"),sQuery(id+"F0.wireOp",EDGE,"E53.1"),sQuery(id+"F0.wireOp",EDGE,"E53.2"),sQuery(id+"F0.wireOp",EDGE,"E54.0"),sQuery(id+"F0.wireOp",EDGE,"E54.1"),sQuery(id+"F0.wireOp",EDGE,"E54.2"),sQuery(id+"F0.wireOp",EDGE,"E55.0"),sQuery(id+"F0.wireOp",EDGE,"E55.1"),sQuery(id+"F0.wireOp",EDGE,"E55.2"),sQuery(id+"F0.wireOp",EDGE,"E56.0"),sQuery(id+"F0.wireOp",EDGE,"E56.1"),sQuery(id+"F0.wireOp",EDGE,"E56.2"),sQuery(id+"F0.wireOp",EDGE,"E57.0"),sQuery(id+"F0.wireOp",EDGE,"E57.1"),sQuery(id+"F0.wireOp",EDGE,"E57.2"),sQuery(id+"F0.wireOp",EDGE,"E59"),sQuery(id+"F0.wireOp",EDGE,"E60"),sQuery(id+"F0.wireOp",EDGE,"E61"),sQuery(id+"F0.wireOp",EDGE,"E62"),sQuery(id+"F0.wireOp",EDGE,"E63"),sQuery(id+"F0.wireOp",EDGE,"E64"),sQuery(id+"F0.wireOp",EDGE,"E65.bottom"),sQuery(id+"F0.wireOp",EDGE,"E65.top"),sQuery(id+"F0.wireOp",EDGE,"E65.left"),sQuery(id+"F0.wireOp",EDGE,"E65.right"),sQuery(id+"F0.wireOp",EDGE,"E66.bottom"),sQuery(id+"F0.wireOp",EDGE,"E66.top"),sQuery(id+"F0.wireOp",EDGE,"E66.left"),sQuery(id+"F0.wireOp",EDGE,"E66.right"),sQuery(id+"F0.wireOp",EDGE,"E67.bottom"),sQuery(id+"F0.wireOp",EDGE,"E67.top"),sQuery(id+"F0.wireOp",EDGE,"E67.left"),sQuery(id+"F0.wireOp",EDGE,"E67.right"),sQuery(id+"F0.wireOp",EDGE,"E68.bottom"),sQuery(id+"F0.wireOp",EDGE,"E68.top"),sQuery(id+"F0.wireOp",EDGE,"E68.left"),sQuery(id+"F0.wireOp",EDGE,"E68.right"),sQuery(id+"F0.wireOp",EDGE,"E69.bottom"),sQuery(id+"F0.wireOp",EDGE,"E69.top"),sQuery(id+"F0.wireOp",EDGE,"E69.left"),sQuery(id+"F0.wireOp",EDGE,"E69.right"),sQuery(id+"F0.wireOp",EDGE,"E70.bottom"),sQuery(id+"F0.wireOp",EDGE,"E70.top"),sQuery(id+"F0.wireOp",EDGE,"E70.left"),sQuery(id+"F0.wireOp",EDGE,"E70.right"),sQuery(id+"F0.wireOp",EDGE,"E71.0"),sQuery(id+"F0.wireOp",EDGE,"E71.1"),sQuery(id+"F0.wireOp",EDGE,"E71.2"),sQuery(id+"F0.wireOp",EDGE,"E71.3"),sQuery(id+"F0.wireOp",EDGE,"E71.4"),sQuery(id+"F0.wireOp",EDGE,"E71.5"),sQuery(id+"F0.wireOp",EDGE,"E72.0"),sQuery(id+"F0.wireOp",EDGE,"E72.1"),sQuery(id+"F0.wireOp",EDGE,"E72.2"),sQuery(id+"F0.wireOp",EDGE,"E72.3"),sQuery(id+"F0.wireOp",EDGE,"E72.4"),sQuery(id+"F0.wireOp",EDGE,"E72.5"),sQuery(id+"F0.wireOp",EDGE,"E73.0"),sQuery(id+"F0.wireOp",EDGE,"E73.1"),sQuery(id+"F0.wireOp",EDGE,"E73.2"),sQuery(id+"F0.wireOp",EDGE,"E73.3"),sQuery(id+"F0.wireOp",EDGE,"E73.4"),sQuery(id+"F0.wireOp",EDGE,"E73.5"),sQuery(id+"F0.wireOp",EDGE,"E74.0"),sQuery(id+"F0.wireOp",EDGE,"E74.1"),sQuery(id+"F0.wireOp",EDGE,"E74.2"),sQuery(id+"F0.wireOp",EDGE,"E74.3"),sQuery(id+"F0.wireOp",EDGE,"E74.4"),sQuery(id+"F0.wireOp",EDGE,"E74.5"),sQuery(id+"F0.wireOp",EDGE,"E75.0"),sQuery(id+"F0.wireOp",EDGE,"E75.1"),sQuery(id+"F0.wireOp",EDGE,"E75.2"),sQuery(id+"F0.wireOp",EDGE,"E75.3"),sQuery(id+"F0.wireOp",EDGE,"E75.4"),sQuery(id+"F0.wireOp",EDGE,"E75.5"),sQuery(id+"F0.wireOp",EDGE,"E76.0"),sQuery(id+"F0.wireOp",EDGE,"E76.1"),sQuery(id+"F0.wireOp",EDGE,"E76.2"),sQuery(id+"F0.wireOp",EDGE,"E76.3"),sQuery(id+"F0.wireOp",EDGE,"E76.4"),sQuery(id+"F0.wireOp",EDGE,"E76.5"),sQuery(id+"F0.wireOp",EDGE,"E77.0"),sQuery(id+"F0.wireOp",EDGE,"E77.1"),sQuery(id+"F0.wireOp",EDGE,"E77.2"),sQuery(id+"F0.wireOp",EDGE,"E77.3"),sQuery(id+"F0.wireOp",EDGE,"E77.4"),sQuery(id+"F0.wireOp",EDGE,"E77.5"),sQuery(id+"F0.wireOp",EDGE,"E78.0"),sQuery(id+"F0.wireOp",EDGE,"E78.1"),sQuery(id+"F0.wireOp",EDGE,"E78.2"),sQuery(id+"F0.wireOp",EDGE,"E78.3"),sQuery(id+"F0.wireOp",EDGE,"E78.4"),sQuery(id+"F0.wireOp",EDGE,"E78.5"),sQuery(id+"F0.wireOp",EDGE,"E79.0"),sQuery(id+"F0.wireOp",EDGE,"E79.1"),sQuery(id+"F0.wireOp",EDGE,"E79.2"),sQuery(id+"F0.wireOp",EDGE,"E79.3"),sQuery(id+"F0.wireOp",EDGE,"E79.4"),sQuery(id+"F0.wireOp",EDGE,"E79.5"),sQuery(id+"F0.wireOp",EDGE,"E80.0"),sQuery(id+"F0.wireOp",EDGE,"E80.1"),sQuery(id+"F0.wireOp",EDGE,"E80.2"),sQuery(id+"F0.wireOp",EDGE,"E80.3"),sQuery(id+"F0.wireOp",EDGE,"E80.4"),sQuery(id+"F0.wireOp",EDGE,"E80.5"),sQuery(id+"F0.wireOp",EDGE,"E81.0"),sQuery(id+"F0.wireOp",EDGE,"E81.1"),sQuery(id+"F0.wireOp",EDGE,"E81.2"),sQuery(id+"F0.wireOp",EDGE,"E81.3"),sQuery(id+"F0.wireOp",EDGE,"E81.4"),sQuery(id+"F0.wireOp",EDGE,"E81.5"),sQuery(id+"F0.wireOp",EDGE,"E82.0"),sQuery(id+"F0.wireOp",EDGE,"E82.1"),sQuery(id+"F0.wireOp",EDGE,"E82.2"),sQuery(id+"F0.wireOp",EDGE,"E82.3"),sQuery(id+"F0.wireOp",EDGE,"E82.4"),sQuery(id+"F0.wireOp",EDGE,"E82.5"),sQuery(id+"F0.wireOp",EDGE,"E83.0"),sQuery(id+"F0.wireOp",EDGE,"E83.1"),sQuery(id+"F0.wireOp",EDGE,"E83.2"),sQuery(id+"F0.wireOp",EDGE,"E83.3"),sQuery(id+"F0.wireOp",EDGE,"E83.4"),sQuery(id+"F0.wireOp",EDGE,"E83.5"),sQuery(id+"F0.wireOp",EDGE,"E84.0"),sQuery(id+"F0.wireOp",EDGE,"E84.1"),sQuery(id+"F0.wireOp",EDGE,"E84.2"),sQuery(id+"F0.wireOp",EDGE,"E84.3"),sQuery(id+"F0.wireOp",EDGE,"E84.4"),sQuery(id+"F0.wireOp",EDGE,"E84.5"),sQuery(id+"F0.wireOp",EDGE,"E85.0"),sQuery(id+"F0.wireOp",EDGE,"E85.1"),sQuery(id+"F0.wireOp",EDGE,"E85.2"),sQuery(id+"F0.wireOp",EDGE,"E85.3"),sQuery(id+"F0.wireOp",EDGE,"E85.4"),sQuery(id+"F0.wireOp",EDGE,"E85.5"),sQuery(id+"F0.wireOp",EDGE,"E86.0"),sQuery(id+"F0.wireOp",EDGE,"E86.1"),sQuery(id+"F0.wireOp",EDGE,"E86.2"),sQuery(id+"F0.wireOp",EDGE,"E86.3"),sQuery(id+"F0.wireOp",EDGE,"E86.4"),sQuery(id+"F0.wireOp",EDGE,"E86.5"),sQuery(id+"F0.wireOp",EDGE,"E87.0"),sQuery(id+"F0.wireOp",EDGE,"E87.1"),sQuery(id+"F0.wireOp",EDGE,"E87.2"),sQuery(id+"F0.wireOp",EDGE,"E87.3"),sQuery(id+"F0.wireOp",EDGE,"E87.4"),sQuery(id+"F0.wireOp",EDGE,"E87.5"),sQuery(id+"F0.wireOp",EDGE,"E88.0"),sQuery(id+"F0.wireOp",EDGE,"E88.1"),sQuery(id+"F0.wireOp",EDGE,"E88.2"),sQuery(id+"F0.wireOp",EDGE,"E88.3"),sQuery(id+"F0.wireOp",EDGE,"E88.4"),sQuery(id+"F0.wireOp",EDGE,"E88.5"),sQuery(id+"F0.wireOp",EDGE,"E89.0"),sQuery(id+"F0.wireOp",EDGE,"E89.1"),sQuery(id+"F0.wireOp",EDGE,"E89.2"),sQuery(id+"F0.wireOp",EDGE,"E89.3"),sQuery(id+"F0.wireOp",EDGE,"E89.4"),sQuery(id+"F0.wireOp",EDGE,"E89.5"),sQuery(id+"F0.wireOp",EDGE,"E90.0"),sQuery(id+"F0.wireOp",EDGE,"E90.1"),sQuery(id+"F0.wireOp",EDGE,"E90.2"),sQuery(id+"F0.wireOp",EDGE,"E90.3"),sQuery(id+"F0.wireOp",EDGE,"E90.4"),sQuery(id+"F0.wireOp",EDGE,"E90.5"),sQuery(id+"F0.wireOp",EDGE,"E91.bottom"),sQuery(id+"F0.wireOp",EDGE,"E91.top"),sQuery(id+"F0.wireOp",EDGE,"E91.left"),sQuery(id+"F0.wireOp",EDGE,"E91.right")])],"isStart":false});
            var sketch = newSketch(context, id + "F2", { "sketchPlane" : qUnion([Q0])});
            skText(sketch, "E92", { "text": "BELLAIR", "fontName": "OpenSans-Regular.ttf"});
            const initialGuessF2  = {"E92": [0.0227, 0.06792, 1, 0, 0.0105]};
            skSetInitialGuess(sketch, initialGuessF2);
            skSolve(sketch);
        }
        {
            var Q0;
            Q0=qSketchRegion(id+"F2",true);
            extrude(context, id + "F3", {"entities" : qUnion([Q0]), "operationType" : NewBodyOperationType.ADD, "depth" : 1 * mm, "offsetDistance" : 25 * mm});
        }
        {
            var Q0;
            {var subQ0=sQuery(id+"F0.wireOp",EDGE,"E69.right");var subQ1=sQuery(id+"F0.wireOp",EDGE,"E69.left");var subQ2=sQuery(id+"F0.wireOp",EDGE,"E69.top");var subQ3=sQuery(id+"F0.wireOp",EDGE,"E69.bottom");var subQ4=sQuery(id+"F0.wireOp",EDGE,"E68.right");var subQ5=sQuery(id+"F0.wireOp",EDGE,"E68.left");var subQ6=sQuery(id+"F0.wireOp",EDGE,"E68.top");var subQ7=sQuery(id+"F0.wireOp",EDGE,"E68.bottom");var subQ8=sQuery(id+"F0.wireOp",EDGE,"E67.right");var subQ9=sQuery(id+"F0.wireOp",EDGE,"E67.left");var subQ10=sQuery(id+"F0.wireOp",EDGE,"E67.top");var subQ11=sQuery(id+"F0.wireOp",EDGE,"E67.bottom");var subQ12=sQuery(id+"F0.wireOp",EDGE,"E66.right");var subQ13=sQuery(id+"F0.wireOp",EDGE,"E66.left");var subQ14=sQuery(id+"F0.wireOp",EDGE,"E66.top");var subQ15=sQuery(id+"F0.wireOp",EDGE,"E66.bottom");var subQ16=sQuery(id+"F0.wireOp",EDGE,"E65.right");var subQ17=sQuery(id+"F0.wireOp",EDGE,"E65.left");var subQ18=sQuery(id+"F0.wireOp",EDGE,"E65.top");var subQ19=sQuery(id+"F0.wireOp",EDGE,"E65.bottom");var subQ20=sQuery(id+"F0.wireOp",EDGE,"E64");var subQ21=sQuery(id+"F0.wireOp",EDGE,"E63");var subQ22=sQuery(id+"F0.wireOp",EDGE,"E62");var subQ23=sQuery(id+"F0.wireOp",EDGE,"E61");var subQ24=sQuery(id+"F0.wireOp",EDGE,"E60");var subQ25=sQuery(id+"F0.wireOp",EDGE,"E59");var subQ26=sQuery(id+"F0.wireOp",EDGE,"E57.2");var subQ27=sQuery(id+"F0.wireOp",EDGE,"E57.1");var subQ28=sQuery(id+"F0.wireOp",EDGE,"E57.0");var subQ29=sQuery(id+"F0.wireOp",EDGE,"E56.2");var subQ30=sQuery(id+"F0.wireOp",EDGE,"E56.1");var subQ31=sQuery(id+"F0.wireOp",EDGE,"E56.0");var subQ32=sQuery(id+"F0.wireOp",EDGE,"E55.2");var subQ33=sQuery(id+"F0.wireOp",EDGE,"E55.1");var subQ34=sQuery(id+"F0.wireOp",EDGE,"E55.0");var subQ35=sQuery(id+"F0.wireOp",EDGE,"E54.2");var subQ36=sQuery(id+"F0.wireOp",EDGE,"E54.1");var subQ37=sQuery(id+"F0.wireOp",EDGE,"E54.0");var subQ38=sQuery(id+"F0.wireOp",EDGE,"E53.2");var subQ39=sQuery(id+"F0.wireOp",EDGE,"E53.1");var subQ40=sQuery(id+"F0.wireOp",EDGE,"E53.0");var subQ41=sQuery(id+"F0.wireOp",EDGE,"E52.2");var subQ42=sQuery(id+"F0.wireOp",EDGE,"E52.1");var subQ43=sQuery(id+"F0.wireOp",EDGE,"E52.0");var subQ44=sQuery(id+"F0.wireOp",EDGE,"E51.right");var subQ45=sQuery(id+"F0.wireOp",EDGE,"E51.left");var subQ46=sQuery(id+"F0.wireOp",EDGE,"E51.top");var subQ47=sQuery(id+"F0.wireOp",EDGE,"E51.bottom");var subQ48=sQuery(id+"F0.wireOp",EDGE,"E50.right");var subQ49=sQuery(id+"F0.wireOp",EDGE,"E50.left");var subQ50=sQuery(id+"F0.wireOp",EDGE,"E50.top");var subQ51=sQuery(id+"F0.wireOp",EDGE,"E50.bottom");var subQ52=sQuery(id+"F0.wireOp",EDGE,"E49.right");var subQ53=sQuery(id+"F0.wireOp",EDGE,"E49.left");var subQ54=sQuery(id+"F0.wireOp",EDGE,"E49.top");var subQ55=sQuery(id+"F0.wireOp",EDGE,"E49.bottom");var subQ56=sQuery(id+"F0.wireOp",EDGE,"E48.right");var subQ57=sQuery(id+"F0.wireOp",EDGE,"E48.left");var subQ58=sQuery(id+"F0.wireOp",EDGE,"E48.top");var subQ59=sQuery(id+"F0.wireOp",EDGE,"E48.bottom");var subQ60=sQuery(id+"F0.wireOp",EDGE,"E47.right");var subQ61=sQuery(id+"F0.wireOp",EDGE,"E47.left");var subQ62=sQuery(id+"F0.wireOp",EDGE,"E47.top");var subQ63=sQuery(id+"F0.wireOp",EDGE,"E47.bottom");var subQ64=sQuery(id+"F0.wireOp",EDGE,"E46.right");var subQ65=sQuery(id+"F0.wireOp",EDGE,"E46.left");var subQ66=sQuery(id+"F0.wireOp",EDGE,"E46.top");var subQ67=sQuery(id+"F0.wireOp",EDGE,"E46.bottom");var subQ68=sQuery(id+"F0.wireOp",EDGE,"E45.right");var subQ69=sQuery(id+"F0.wireOp",EDGE,"E45.left");var subQ70=sQuery(id+"F0.wireOp",EDGE,"E45.top");var subQ71=sQuery(id+"F0.wireOp",EDGE,"E45.bottom");var subQ72=sQuery(id+"F0.wireOp",EDGE,"E44.right");var subQ73=sQuery(id+"F0.wireOp",EDGE,"E44.left");var subQ74=sQuery(id+"F0.wireOp",EDGE,"E44.top");var subQ75=sQuery(id+"F0.wireOp",EDGE,"E44.bottom");var subQ76=sQuery(id+"F0.wireOp",EDGE,"E43.right");var subQ77=sQuery(id+"F0.wireOp",EDGE,"E43.left");var subQ78=sQuery(id+"F0.wireOp",EDGE,"E43.top");var subQ79=sQuery(id+"F0.wireOp",EDGE,"E43.bottom");var subQ80=sQuery(id+"F0.wireOp",EDGE,"E42.right");var subQ81=sQuery(id+"F0.wireOp",EDGE,"E42.left");var subQ82=sQuery(id+"F0.wireOp",EDGE,"E42.top");var subQ83=sQuery(id+"F0.wireOp",EDGE,"E42.bottom");var subQ84=sQuery(id+"F0.wireOp",EDGE,"E41.2");var subQ85=sQuery(id+"F0.wireOp",EDGE,"E41.1");var subQ86=sQuery(id+"F0.wireOp",EDGE,"E41.0");var subQ87=sQuery(id+"F0.wireOp",EDGE,"E40.2");var subQ88=sQuery(id+"F0.wireOp",EDGE,"E40.1");var subQ89=sQuery(id+"F0.wireOp",EDGE,"E40.0");var subQ90=sQuery(id+"F0.wireOp",EDGE,"E39.2");var subQ91=sQuery(id+"F0.wireOp",EDGE,"E39.1");var subQ92=sQuery(id+"F0.wireOp",EDGE,"E39.0");var subQ93=sQuery(id+"F0.wireOp",EDGE,"E38.2");var subQ94=sQuery(id+"F0.wireOp",EDGE,"E38.1");var subQ95=sQuery(id+"F0.wireOp",EDGE,"E38.0");var subQ96=sQuery(id+"F0.wireOp",EDGE,"E37.2");var subQ97=sQuery(id+"F0.wireOp",EDGE,"E37.1");var subQ98=sQuery(id+"F0.wireOp",EDGE,"E37.0");var subQ99=sQuery(id+"F0.wireOp",EDGE,"E36.2");var subQ100=sQuery(id+"F0.wireOp",EDGE,"E16.top");var subQ101=sQuery(id+"F0.wireOp",EDGE,"E16.bottom");var subQ102=sQuery(id+"F0.wireOp",EDGE,"E15.right");var subQ103=sQuery(id+"F0.wireOp",EDGE,"E15.left");var subQ104=sQuery(id+"F0.wireOp",EDGE,"E15.top");var subQ105=sQuery(id+"F0.wireOp",EDGE,"E15.bottom");var subQ106=sQuery(id+"F0.wireOp",EDGE,"E14.right");var subQ107=sQuery(id+"F0.wireOp",EDGE,"E14.left");var subQ108=sQuery(id+"F0.wireOp",EDGE,"E14.top");var subQ109=sQuery(id+"F0.wireOp",EDGE,"E14.bottom");var subQ110=sQuery(id+"F0.wireOp",EDGE,"E13");var subQ111=sQuery(id+"F0.wireOp",EDGE,"E12");var subQ112=sQuery(id+"F0.wireOp",EDGE,"E11");var subQ113=sQuery(id+"F0.wireOp",EDGE,"E10");var subQ114=sQuery(id+"F0.wireOp",EDGE,"E9");var subQ115=sQuery(id+"F0.wireOp",EDGE,"E8");var subQ116=sQuery(id+"F0.wireOp",EDGE,"E7");var subQ117=sQuery(id+"F0.wireOp",EDGE,"E6.right");var subQ118=sQuery(id+"F0.wireOp",EDGE,"E6.left");var subQ119=sQuery(id+"F0.wireOp",EDGE,"E6.top");var subQ120=sQuery(id+"F0.wireOp",EDGE,"E6.bottom");var subQ121=sQuery(id+"F0.wireOp",EDGE,"E5.right");var subQ122=sQuery(id+"F0.wireOp",EDGE,"E5.left");var subQ123=sQuery(id+"F0.wireOp",EDGE,"E2.bottom");var subQ124=sQuery(id+"F0.wireOp",EDGE,"E1.right");var subQ125=sQuery(id+"F0.wireOp",EDGE,"E1.left");var subQ126=sQuery(id+"F0.wireOp",EDGE,"E1.top");var subQ127=sQuery(id+"F0.wireOp",EDGE,"E71.1");var subQ128=sQuery(id+"F0.wireOp",EDGE,"E1.bottom");var subQ129=sQuery(id+"F0.wireOp",EDGE,"E2.top");var subQ130=sQuery(id+"F0.wireOp",EDGE,"E16.left");var subQ131=sQuery(id+"F0.wireOp",EDGE,"E0.bottom");var subQ132=sQuery(id+"F0.wireOp",EDGE,"E36.1");var subQ133=sQuery(id+"F0.wireOp",EDGE,"E5.top");var subQ134=sQuery(id+"F0.wireOp",EDGE,"E71.0");var subQ135=sQuery(id+"F0.wireOp",EDGE,"E0.right");var subQ136=sQuery(id+"F0.wireOp",EDGE,"E0.top");var subQ137=sQuery(id+"F0.wireOp",EDGE,"E0.left");var subQ138=sQuery(id+"F0.wireOp",EDGE,"E2.left");var subQ139=sQuery(id+"F0.wireOp",EDGE,"E2.right");var subQ140=sQuery(id+"F0.wireOp",EDGE,"E3.bottom");var subQ141=sQuery(id+"F0.wireOp",EDGE,"E3.top");var subQ142=sQuery(id+"F0.wireOp",EDGE,"E3.left");var subQ143=sQuery(id+"F0.wireOp",EDGE,"E3.right");var subQ144=sQuery(id+"F0.wireOp",EDGE,"E4.bottom");var subQ145=sQuery(id+"F0.wireOp",EDGE,"E4.top");var subQ146=sQuery(id+"F0.wireOp",EDGE,"E4.left");var subQ147=sQuery(id+"F0.wireOp",EDGE,"E4.right");var subQ148=sQuery(id+"F0.wireOp",EDGE,"E5.bottom");var subQ149=sQuery(id+"F0.wireOp",EDGE,"E16.right");var subQ150=sQuery(id+"F0.wireOp",EDGE,"E17.bottom");var subQ151=sQuery(id+"F0.wireOp",EDGE,"E17.top");var subQ152=sQuery(id+"F0.wireOp",EDGE,"E17.left");var subQ153=sQuery(id+"F0.wireOp",EDGE,"E17.right");var subQ154=sQuery(id+"F0.wireOp",EDGE,"E18.bottom");var subQ155=sQuery(id+"F0.wireOp",EDGE,"E18.top");var subQ156=sQuery(id+"F0.wireOp",EDGE,"E18.left");var subQ157=sQuery(id+"F0.wireOp",EDGE,"E18.right");var subQ158=sQuery(id+"F0.wireOp",EDGE,"E19.bottom");var subQ159=sQuery(id+"F0.wireOp",EDGE,"E19.top");var subQ160=sQuery(id+"F0.wireOp",EDGE,"E19.left");var subQ161=sQuery(id+"F0.wireOp",EDGE,"E19.right");var subQ162=sQuery(id+"F0.wireOp",EDGE,"E20.bottom");var subQ163=sQuery(id+"F0.wireOp",EDGE,"E20.top");var subQ164=sQuery(id+"F0.wireOp",EDGE,"E20.left");var subQ165=sQuery(id+"F0.wireOp",EDGE,"E20.right");var subQ166=sQuery(id+"F0.wireOp",EDGE,"E21");var subQ167=sQuery(id+"F0.wireOp",EDGE,"E22");var subQ168=sQuery(id+"F0.wireOp",EDGE,"E23");var subQ169=sQuery(id+"F0.wireOp",EDGE,"E24");var subQ170=sQuery(id+"F0.wireOp",EDGE,"E25");var subQ171=sQuery(id+"F0.wireOp",EDGE,"E26");var subQ172=sQuery(id+"F0.wireOp",EDGE,"E27");var subQ173=sQuery(id+"F0.wireOp",EDGE,"E28.0");var subQ174=sQuery(id+"F0.wireOp",EDGE,"E28.1");var subQ175=sQuery(id+"F0.wireOp",EDGE,"E28.2");var subQ176=sQuery(id+"F0.wireOp",EDGE,"E29.0");var subQ177=sQuery(id+"F0.wireOp",EDGE,"E29.1");var subQ178=sQuery(id+"F0.wireOp",EDGE,"E29.2");var subQ179=sQuery(id+"F0.wireOp",EDGE,"E30.0");var subQ180=sQuery(id+"F0.wireOp",EDGE,"E30.1");var subQ181=sQuery(id+"F0.wireOp",EDGE,"E30.2");var subQ182=sQuery(id+"F0.wireOp",EDGE,"E31.0");var subQ183=sQuery(id+"F0.wireOp",EDGE,"E31.1");var subQ184=sQuery(id+"F0.wireOp",EDGE,"E31.2");var subQ185=sQuery(id+"F0.wireOp",EDGE,"E32.0");var subQ186=sQuery(id+"F0.wireOp",EDGE,"E32.1");var subQ187=sQuery(id+"F0.wireOp",EDGE,"E32.2");var subQ188=sQuery(id+"F0.wireOp",EDGE,"E33.0");var subQ189=sQuery(id+"F0.wireOp",EDGE,"E33.1");var subQ190=sQuery(id+"F0.wireOp",EDGE,"E33.2");var subQ191=sQuery(id+"F0.wireOp",EDGE,"E34.0");var subQ192=sQuery(id+"F0.wireOp",EDGE,"E34.1");var subQ193=sQuery(id+"F0.wireOp",EDGE,"E34.2");var subQ194=sQuery(id+"F0.wireOp",EDGE,"E35.0");var subQ195=sQuery(id+"F0.wireOp",EDGE,"E35.1");var subQ196=sQuery(id+"F0.wireOp",EDGE,"E35.2");var subQ197=sQuery(id+"F0.wireOp",EDGE,"E36.0");var subQ198=sQuery(id+"F0.wireOp",EDGE,"E71.2");var subQ199=sQuery(id+"F0.wireOp",EDGE,"E71.3");var subQ200=sQuery(id+"F0.wireOp",EDGE,"E71.4");var subQ201=sQuery(id+"F0.wireOp",EDGE,"E71.5");var subQ202=sQuery(id+"F0.wireOp",EDGE,"E72.0");var subQ203=sQuery(id+"F0.wireOp",EDGE,"E72.1");var subQ204=sQuery(id+"F0.wireOp",EDGE,"E72.2");var subQ205=sQuery(id+"F0.wireOp",EDGE,"E72.3");var subQ206=sQuery(id+"F0.wireOp",EDGE,"E72.4");var subQ207=sQuery(id+"F0.wireOp",EDGE,"E72.5");var subQ208=sQuery(id+"F0.wireOp",EDGE,"E73.0");var subQ209=sQuery(id+"F0.wireOp",EDGE,"E73.1");var subQ210=sQuery(id+"F0.wireOp",EDGE,"E73.2");var subQ211=sQuery(id+"F0.wireOp",EDGE,"E73.3");var subQ212=sQuery(id+"F0.wireOp",EDGE,"E73.4");var subQ213=sQuery(id+"F0.wireOp",EDGE,"E73.5");var subQ214=sQuery(id+"F0.wireOp",EDGE,"E74.0");var subQ215=sQuery(id+"F0.wireOp",EDGE,"E74.1");var subQ216=sQuery(id+"F0.wireOp",EDGE,"E74.2");var subQ217=sQuery(id+"F0.wireOp",EDGE,"E74.3");var subQ218=sQuery(id+"F0.wireOp",EDGE,"E74.4");var subQ219=sQuery(id+"F0.wireOp",EDGE,"E74.5");var subQ220=sQuery(id+"F0.wireOp",EDGE,"E75.0");var subQ221=sQuery(id+"F0.wireOp",EDGE,"E75.1");var subQ222=sQuery(id+"F0.wireOp",EDGE,"E75.2");var subQ223=sQuery(id+"F0.wireOp",EDGE,"E75.3");var subQ224=sQuery(id+"F0.wireOp",EDGE,"E75.4");var subQ225=sQuery(id+"F0.wireOp",EDGE,"E75.5");var subQ226=sQuery(id+"F0.wireOp",EDGE,"E76.0");var subQ227=sQuery(id+"F0.wireOp",EDGE,"E76.1");var subQ228=sQuery(id+"F0.wireOp",EDGE,"E76.2");var subQ229=sQuery(id+"F0.wireOp",EDGE,"E76.3");var subQ230=sQuery(id+"F0.wireOp",EDGE,"E76.4");var subQ231=sQuery(id+"F0.wireOp",EDGE,"E76.5");var subQ232=sQuery(id+"F0.wireOp",EDGE,"E77.0");var subQ233=sQuery(id+"F0.wireOp",EDGE,"E77.1");var subQ234=sQuery(id+"F0.wireOp",EDGE,"E77.2");var subQ235=sQuery(id+"F0.wireOp",EDGE,"E77.3");var subQ236=sQuery(id+"F0.wireOp",EDGE,"E77.4");var subQ237=sQuery(id+"F0.wireOp",EDGE,"E77.5");var subQ238=sQuery(id+"F0.wireOp",EDGE,"E78.0");var subQ239=sQuery(id+"F0.wireOp",EDGE,"E78.1");var subQ240=sQuery(id+"F0.wireOp",EDGE,"E78.2");var subQ241=sQuery(id+"F0.wireOp",EDGE,"E78.3");var subQ242=sQuery(id+"F0.wireOp",EDGE,"E78.4");var subQ243=sQuery(id+"F0.wireOp",EDGE,"E78.5");var subQ244=sQuery(id+"F0.wireOp",EDGE,"E79.0");var subQ245=sQuery(id+"F0.wireOp",EDGE,"E79.1");var subQ246=sQuery(id+"F0.wireOp",EDGE,"E79.2");var subQ247=sQuery(id+"F0.wireOp",EDGE,"E79.3");var subQ248=sQuery(id+"F0.wireOp",EDGE,"E79.4");var subQ249=sQuery(id+"F0.wireOp",EDGE,"E79.5");var subQ250=sQuery(id+"F0.wireOp",EDGE,"E80.0");var subQ251=sQuery(id+"F0.wireOp",EDGE,"E80.1");var subQ252=sQuery(id+"F0.wireOp",EDGE,"E80.2");var subQ253=sQuery(id+"F0.wireOp",EDGE,"E80.3");var subQ254=sQuery(id+"F0.wireOp",EDGE,"E80.4");var subQ255=sQuery(id+"F0.wireOp",EDGE,"E80.5");var subQ256=sQuery(id+"F0.wireOp",EDGE,"E81.0");var subQ257=sQuery(id+"F0.wireOp",EDGE,"E81.1");var subQ258=sQuery(id+"F0.wireOp",EDGE,"E81.2");var subQ259=sQuery(id+"F0.wireOp",EDGE,"E81.3");var subQ260=sQuery(id+"F0.wireOp",EDGE,"E81.4");var subQ261=sQuery(id+"F0.wireOp",EDGE,"E81.5");var subQ262=sQuery(id+"F0.wireOp",EDGE,"E82.0");var subQ263=sQuery(id+"F0.wireOp",EDGE,"E82.1");var subQ264=sQuery(id+"F0.wireOp",EDGE,"E82.2");var subQ265=sQuery(id+"F0.wireOp",EDGE,"E82.3");var subQ266=sQuery(id+"F0.wireOp",EDGE,"E82.4");var subQ267=sQuery(id+"F0.wireOp",EDGE,"E82.5");var subQ268=sQuery(id+"F0.wireOp",EDGE,"E83.0");var subQ269=sQuery(id+"F0.wireOp",EDGE,"E83.1");var subQ270=sQuery(id+"F0.wireOp",EDGE,"E83.2");var subQ271=sQuery(id+"F0.wireOp",EDGE,"E83.3");var subQ272=sQuery(id+"F0.wireOp",EDGE,"E83.4");var subQ273=sQuery(id+"F0.wireOp",EDGE,"E83.5");var subQ274=sQuery(id+"F0.wireOp",EDGE,"E84.0");var subQ275=sQuery(id+"F0.wireOp",EDGE,"E84.1");var subQ276=sQuery(id+"F0.wireOp",EDGE,"E84.2");var subQ277=sQuery(id+"F0.wireOp",EDGE,"E84.3");var subQ278=sQuery(id+"F0.wireOp",EDGE,"E84.4");var subQ279=sQuery(id+"F0.wireOp",EDGE,"E84.5");var subQ280=sQuery(id+"F0.wireOp",EDGE,"E85.0");var subQ281=sQuery(id+"F0.wireOp",EDGE,"E85.1");var subQ282=sQuery(id+"F0.wireOp",EDGE,"E85.2");var subQ283=sQuery(id+"F0.wireOp",EDGE,"E85.3");var subQ284=sQuery(id+"F0.wireOp",EDGE,"E85.4");var subQ285=sQuery(id+"F0.wireOp",EDGE,"E85.5");var subQ286=sQuery(id+"F0.wireOp",EDGE,"E86.0");var subQ287=sQuery(id+"F0.wireOp",EDGE,"E86.1");var subQ288=sQuery(id+"F0.wireOp",EDGE,"E86.2");var subQ289=sQuery(id+"F0.wireOp",EDGE,"E86.3");var subQ290=sQuery(id+"F0.wireOp",EDGE,"E86.4");var subQ291=sQuery(id+"F0.wireOp",EDGE,"E86.5");var subQ292=sQuery(id+"F0.wireOp",EDGE,"E87.0");var subQ293=sQuery(id+"F0.wireOp",EDGE,"E87.1");var subQ294=sQuery(id+"F0.wireOp",EDGE,"E87.2");var subQ295=sQuery(id+"F0.wireOp",EDGE,"E87.3");var subQ296=sQuery(id+"F0.wireOp",EDGE,"E87.4");var subQ297=sQuery(id+"F0.wireOp",EDGE,"E87.5");var subQ298=sQuery(id+"F0.wireOp",EDGE,"E88.0");var subQ299=sQuery(id+"F0.wireOp",EDGE,"E88.1");var subQ300=sQuery(id+"F0.wireOp",EDGE,"E88.2");var subQ301=sQuery(id+"F0.wireOp",EDGE,"E88.3");var subQ302=sQuery(id+"F0.wireOp",EDGE,"E88.4");var subQ303=sQuery(id+"F0.wireOp",EDGE,"E88.5");var subQ304=sQuery(id+"F0.wireOp",EDGE,"E89.0");var subQ305=sQuery(id+"F0.wireOp",EDGE,"E89.1");var subQ306=sQuery(id+"F0.wireOp",EDGE,"E89.2");var subQ307=sQuery(id+"F0.wireOp",EDGE,"E89.3");var subQ308=sQuery(id+"F0.wireOp",EDGE,"E89.4");var subQ309=sQuery(id+"F0.wireOp",EDGE,"E89.5");var subQ310=sQuery(id+"F0.wireOp",EDGE,"E90.0");var subQ311=sQuery(id+"F0.wireOp",EDGE,"E90.1");var subQ312=sQuery(id+"F0.wireOp",EDGE,"E90.2");var subQ313=sQuery(id+"F0.wireOp",EDGE,"E90.3");var subQ314=sQuery(id+"F0.wireOp",EDGE,"E90.4");var subQ315=sQuery(id+"F0.wireOp",EDGE,"E90.5");var subQ316=sQuery(id+"F0.wireOp",EDGE,"E91.bottom");var subQ317=sQuery(id+"F0.wireOp",EDGE,"E91.top");var subQ318=sQuery(id+"F0.wireOp",EDGE,"E91.left");var subQ319=sQuery(id+"F0.wireOp",EDGE,"E91.right");Q0=makeQuery(id+"F3.boolean.opBoolean","SPLIT",FACE,{"disambiguationData":[TD([makeQuery(id+"F1.opExtrude","SWEPT_FACE",FACE,{"disambiguationData":[OSD([subQ131])]})])],"derivedFrom":makeQuery(id+"F1.opExtrude","CAP_FACE",FACE,{"disambiguationData":[OSD([subQ131,subQ136,subQ137,subQ135,subQ128,subQ126,subQ125,subQ124,subQ123,subQ129,subQ138,subQ139,subQ140,subQ141,subQ142,subQ143,subQ144,subQ145,subQ146,subQ147,subQ148,subQ133,subQ122,subQ121,subQ120,subQ119,subQ118,subQ117,subQ116,subQ115,subQ114,subQ113,subQ112,subQ111,subQ110,subQ109,subQ108,subQ107,subQ106,subQ105,subQ104,subQ103,subQ102,subQ101,subQ100,subQ130,subQ149,subQ150,subQ151,subQ152,subQ153,subQ154,subQ155,subQ156,subQ157,subQ158,subQ159,subQ160,subQ161,subQ162,subQ163,subQ164,subQ165,subQ166,subQ167,subQ168,subQ169,subQ170,subQ171,subQ172,subQ173,subQ174,subQ175,subQ176,subQ177,subQ178,subQ179,subQ180,subQ181,subQ182,subQ183,subQ184,subQ185,subQ186,subQ187,subQ188,subQ189,subQ190,subQ191,subQ192,subQ193,subQ194,subQ195,subQ196,subQ197,subQ132,subQ99,subQ98,subQ97,subQ96,subQ95,subQ94,subQ93,subQ92,subQ91,subQ90,subQ89,subQ88,subQ87,subQ86,subQ85,subQ84,subQ83,subQ82,subQ81,subQ80,subQ79,subQ78,subQ77,subQ76,subQ75,subQ74,subQ73,subQ72,subQ71,subQ70,subQ69,subQ68,subQ67,subQ66,subQ65,subQ64,subQ63,subQ62,subQ61,subQ60,subQ59,subQ58,subQ57,subQ56,subQ55,subQ54,subQ53,subQ52,subQ51,subQ50,subQ49,subQ48,subQ47,subQ46,subQ45,subQ44,subQ43,subQ42,subQ41,subQ40,subQ39,subQ38,subQ37,subQ36,subQ35,subQ34,subQ33,subQ32,subQ31,subQ30,subQ29,subQ28,subQ27,subQ26,subQ25,subQ24,subQ23,subQ22,subQ21,subQ20,subQ19,subQ18,subQ17,subQ16,subQ15,subQ14,subQ13,subQ12,subQ11,subQ10,subQ9,subQ8,subQ7,subQ6,subQ5,subQ4,subQ3,subQ2,subQ1,subQ0,subQ134,subQ127,subQ198,subQ199,subQ200,subQ201,subQ202,subQ203,subQ204,subQ205,subQ206,subQ207,subQ208,subQ209,subQ210,subQ211,subQ212,subQ213,subQ214,subQ215,subQ216,subQ217,subQ218,subQ219,subQ220,subQ221,subQ222,subQ223,subQ224,subQ225,subQ226,subQ227,subQ228,subQ229,subQ230,subQ231,subQ232,subQ233,subQ234,subQ235,subQ236,subQ237,subQ238,subQ239,subQ240,subQ241,subQ242,subQ243,subQ244,subQ245,subQ246,subQ247,subQ248,subQ249,subQ250,subQ251,subQ252,subQ253,subQ254,subQ255,subQ256,subQ257,subQ258,subQ259,subQ260,subQ261,subQ262,subQ263,subQ264,subQ265,subQ266,subQ267,subQ268,subQ269,subQ270,subQ271,subQ272,subQ273,subQ274,subQ275,subQ276,subQ277,subQ278,subQ279,subQ280,subQ281,subQ282,subQ283,subQ284,subQ285,subQ286,subQ287,subQ288,subQ289,subQ290,subQ291,subQ292,subQ293,subQ294,subQ295,subQ296,subQ297,subQ298,subQ299,subQ300,subQ301,subQ302,subQ303,subQ304,subQ305,subQ306,subQ307,subQ308,subQ309,subQ310,subQ311,subQ312,subQ313,subQ314,subQ315,subQ316,subQ317,subQ318,subQ319])],"isStart":false})});}
            var sketch = newSketch(context, id + "F4", { "sketchPlane" : qUnion([Q0])});
            skText(sketch, "E93", { "text": "q-_-p", "fontName": "OpenSans-Bold.ttf"});
            const initialGuessF4  = {"E93": [0.1149, -0.00409, 1, 0, 0.00403]};
            skSetInitialGuess(sketch, initialGuessF4);
            skSolve(sketch);
        }
        {
            var Q0;
            Q0=qSketchRegion(id+"F4",true);
            extrude(context, id + "F5", {"entities" : qUnion([Q0]), "operationType" : NewBodyOperationType.ADD, "depth" : 1 * mm, "offsetDistance" : 25 * mm});
        }
    });
